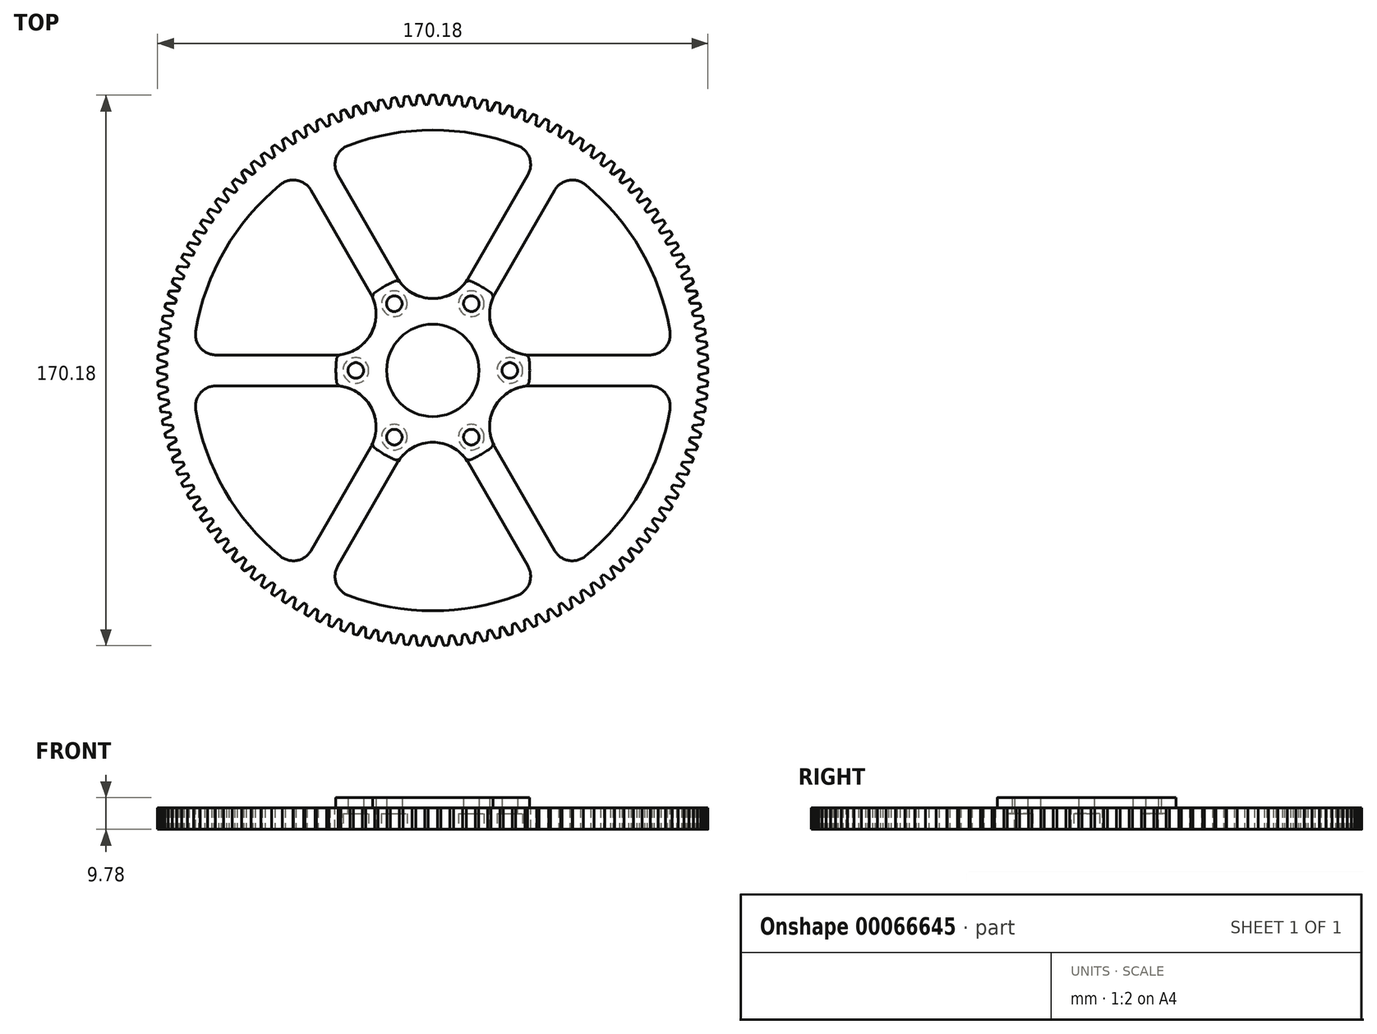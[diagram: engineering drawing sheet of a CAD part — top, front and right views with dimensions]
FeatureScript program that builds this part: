
annotation { "Feature Type Name" : "Feature", "Feature Type Description" : "" }
export const myFeature = defineFeature(function(context is Context, id is Id, definition is map)
    precondition{}
    {
        {
            var Q0;
            Q0=qCreatedBy(makeId("Top.planeOp"),FACE);
            var sketch = newSketch(context, id + "F0", { "sketchPlane" : qUnion([Q0])});
            skArc(sketch, "E0", {"start": v(-1.4, 82.23) * mm, "mid": v(-82.23, -1.4) * mm, "end": v(1.4, -82.23) * mm});
            skArc(sketch, "E1", {"start": v(1.4, -82.23) * mm, "mid": v(82.24, 0) * mm, "end": v(1.4, 82.23) * mm});
            skLineSegment(sketch, "E2", {"start": v(1.4, 82.23) * mm, "end": v(0.7, 84.97) * mm});
            skArc(sketch, "E3", {"start": v(0.7, 84.97) * mm, "mid": v(0.64, 85.06) * mm, "end": v(0.55, 85.1) * mm});
            skLineSegment(sketch, "E4", {"start": v(-1.4, 82.23) * mm, "end": v(-0.7, 84.97) * mm});
            skArc(sketch, "E5", {"start": v(-0.55, 85.1) * mm, "mid": v(-0.64, 85.06) * mm, "end": v(-0.7, 84.97) * mm});
            skLineSegment(sketch, "E6", {"start": v(-0.55, 85.1) * mm, "end": v(0.55, 85.1) * mm});
            skArc(sketch, "E7", {"start": v(1.4, 82.23) * mm, "mid": v(0, 82.24) * mm, "end": v(-1.4, 82.23) * mm});
            skSolve(sketch);
        }
        {
            var Q0;
            Q0=makeQuery(id+"F0.imprint","IMPRINT",FACE,{"disambiguationData":[TD([[makeQuery(id+"F0.imprint","IMPRINT",EDGE,{"derivedFrom":sQuery(id+"F0.wireOp",EDGE,"E0")}),1.0]])]});
            extrude(context, id + "F1", {"entities" : qUnion([Q0]), "endBound" : BoundingType.SYMMETRIC, "depth" : 6.6 * mm});
        }
        {
            var Q0;
            Q0=makeQuery(id+"F0.imprint","IMPRINT",FACE,{"disambiguationData":[TD([[makeQuery(id+"F0.imprint","IMPRINT",EDGE,{"derivedFrom":sQuery(id+"F0.wireOp",EDGE,"E2")}),1.0]])]});
            var Q1;
            Q1=makeQuery(id+"F1.opExtrude","CAP_FACE",FACE,{"disambiguationData":[OSD([sQuery(id+"F0.wireOp",EDGE,"E0"),sQuery(id+"F0.wireOp",EDGE,"E1"),sQuery(id+"F0.wireOp",EDGE,"E7")])],"isStart":false});
            var Q2;
            Q2=makeQuery(id+"F1.opExtrude","CAP_FACE",FACE,{"disambiguationData":[OSD([sQuery(id+"F0.wireOp",EDGE,"E0"),sQuery(id+"F0.wireOp",EDGE,"E1"),sQuery(id+"F0.wireOp",EDGE,"E7")])],"isStart":true});
            extrude(context, id + "F2", {"entities" : qUnion([Q0]), "endBound" : BoundingType.UP_TO_SURFACE, "endBoundEntityFace" : qUnion([Q1]), "depth" : 25.4 * mm, "hasSecondDirection" : true, "secondDirectionBound" : SecondDirectionBoundingType.UP_TO_SURFACE, "secondDirectionOppositeDirection" : true, "secondDirectionBoundEntityFace" : qUnion([Q2]), "secondDirectionDepth" : 25.4 * mm});
        }
        {
            var Q0;
            Q0=makeQuery(id+"F2.opExtrude","SWEPT_BODY",BODY,{"disambiguationData":[OSD([sQuery(id+"F0.wireOp",EDGE,"E2"),sQuery(id+"F0.wireOp",EDGE,"E3"),sQuery(id+"F0.wireOp",EDGE,"E4"),sQuery(id+"F0.wireOp",EDGE,"E5"),sQuery(id+"F0.wireOp",EDGE,"E6"),sQuery(id+"F0.wireOp",EDGE,"E7")])]});
            var Q1;
            Q1=makeQuery(id+"F1.opExtrude","CAP_EDGE",EDGE,{"disambiguationData":[OSD([sQuery(id+"F0.wireOp",EDGE,"E0"),sQuery(id+"F0.wireOp",EDGE,"E1"),sQuery(id+"F0.wireOp",EDGE,"E7")])],"isStart":false});
            circularPattern(context, id + "F3", {"operationType" : NewBodyOperationType.ADD, "entities" : qUnion([Q0]), "axis" : qUnion([Q1]), "angle" : 360 * degree, "instanceCount" : 132, "oppositeDirection" : true, "equalSpace" : true});
        }
        {
            var Q0;
            {var subQ0=sQuery(id+"F0.wireOp",EDGE,"E7");var subQ1=makeQuery(id+"F2.opExtrude","CAP_FACE",FACE,{"disambiguationData":[OSD([sQuery(id+"F0.wireOp",EDGE,"E2"),sQuery(id+"F0.wireOp",EDGE,"E3"),sQuery(id+"F0.wireOp",EDGE,"E4"),sQuery(id+"F0.wireOp",EDGE,"E5"),sQuery(id+"F0.wireOp",EDGE,"E6"),subQ0])],"isStart":false});Q0=makeQuery(id+"F3.boolean.opBoolean","MERGE",FACE,{"derivedFrom":[makeQuery(id+"F1.opExtrude","CAP_FACE",FACE,{"disambiguationData":[OSD([sQuery(id+"F0.wireOp",EDGE,"E0"),sQuery(id+"F0.wireOp",EDGE,"E1"),subQ0])],"isStart":false}),subQ1,makeQuery(id+"F3.opPattern","COPY",FACE,{"derivedFrom":subQ1,"instanceName":"1"}),makeQuery(id+"F3.opPattern","COPY",FACE,{"derivedFrom":subQ1,"instanceName":"2"}),makeQuery(id+"F3.opPattern","COPY",FACE,{"derivedFrom":subQ1,"instanceName":"3"}),makeQuery(id+"F3.opPattern","COPY",FACE,{"derivedFrom":subQ1,"instanceName":"4"}),makeQuery(id+"F3.opPattern","COPY",FACE,{"derivedFrom":subQ1,"instanceName":"5"}),makeQuery(id+"F3.opPattern","COPY",FACE,{"derivedFrom":subQ1,"instanceName":"6"}),makeQuery(id+"F3.opPattern","COPY",FACE,{"derivedFrom":subQ1,"instanceName":"7"}),makeQuery(id+"F3.opPattern","COPY",FACE,{"derivedFrom":subQ1,"instanceName":"8"}),makeQuery(id+"F3.opPattern","COPY",FACE,{"derivedFrom":subQ1,"instanceName":"9"}),makeQuery(id+"F3.opPattern","COPY",FACE,{"derivedFrom":subQ1,"instanceName":"10"}),makeQuery(id+"F3.opPattern","COPY",FACE,{"derivedFrom":subQ1,"instanceName":"11"}),makeQuery(id+"F3.opPattern","COPY",FACE,{"derivedFrom":subQ1,"instanceName":"12"}),makeQuery(id+"F3.opPattern","COPY",FACE,{"derivedFrom":subQ1,"instanceName":"13"}),makeQuery(id+"F3.opPattern","COPY",FACE,{"derivedFrom":subQ1,"instanceName":"14"}),makeQuery(id+"F3.opPattern","COPY",FACE,{"derivedFrom":subQ1,"instanceName":"15"}),makeQuery(id+"F3.opPattern","COPY",FACE,{"derivedFrom":subQ1,"instanceName":"16"}),makeQuery(id+"F3.opPattern","COPY",FACE,{"derivedFrom":subQ1,"instanceName":"17"}),makeQuery(id+"F3.opPattern","COPY",FACE,{"derivedFrom":subQ1,"instanceName":"18"}),makeQuery(id+"F3.opPattern","COPY",FACE,{"derivedFrom":subQ1,"instanceName":"19"}),makeQuery(id+"F3.opPattern","COPY",FACE,{"derivedFrom":subQ1,"instanceName":"20"}),makeQuery(id+"F3.opPattern","COPY",FACE,{"derivedFrom":subQ1,"instanceName":"21"}),makeQuery(id+"F3.opPattern","COPY",FACE,{"derivedFrom":subQ1,"instanceName":"22"}),makeQuery(id+"F3.opPattern","COPY",FACE,{"derivedFrom":subQ1,"instanceName":"23"}),makeQuery(id+"F3.opPattern","COPY",FACE,{"derivedFrom":subQ1,"instanceName":"24"}),makeQuery(id+"F3.opPattern","COPY",FACE,{"derivedFrom":subQ1,"instanceName":"25"}),makeQuery(id+"F3.opPattern","COPY",FACE,{"derivedFrom":subQ1,"instanceName":"26"}),makeQuery(id+"F3.opPattern","COPY",FACE,{"derivedFrom":subQ1,"instanceName":"27"}),makeQuery(id+"F3.opPattern","COPY",FACE,{"derivedFrom":subQ1,"instanceName":"28"}),makeQuery(id+"F3.opPattern","COPY",FACE,{"derivedFrom":subQ1,"instanceName":"29"}),makeQuery(id+"F3.opPattern","COPY",FACE,{"derivedFrom":subQ1,"instanceName":"30"}),makeQuery(id+"F3.opPattern","COPY",FACE,{"derivedFrom":subQ1,"instanceName":"31"}),makeQuery(id+"F3.opPattern","COPY",FACE,{"derivedFrom":subQ1,"instanceName":"32"}),makeQuery(id+"F3.opPattern","COPY",FACE,{"derivedFrom":subQ1,"instanceName":"33"}),makeQuery(id+"F3.opPattern","COPY",FACE,{"derivedFrom":subQ1,"instanceName":"34"}),makeQuery(id+"F3.opPattern","COPY",FACE,{"derivedFrom":subQ1,"instanceName":"35"}),makeQuery(id+"F3.opPattern","COPY",FACE,{"derivedFrom":subQ1,"instanceName":"36"}),makeQuery(id+"F3.opPattern","COPY",FACE,{"derivedFrom":subQ1,"instanceName":"37"}),makeQuery(id+"F3.opPattern","COPY",FACE,{"derivedFrom":subQ1,"instanceName":"38"}),makeQuery(id+"F3.opPattern","COPY",FACE,{"derivedFrom":subQ1,"instanceName":"39"}),makeQuery(id+"F3.opPattern","COPY",FACE,{"derivedFrom":subQ1,"instanceName":"40"}),makeQuery(id+"F3.opPattern","COPY",FACE,{"derivedFrom":subQ1,"instanceName":"41"}),makeQuery(id+"F3.opPattern","COPY",FACE,{"derivedFrom":subQ1,"instanceName":"42"}),makeQuery(id+"F3.opPattern","COPY",FACE,{"derivedFrom":subQ1,"instanceName":"43"}),makeQuery(id+"F3.opPattern","COPY",FACE,{"derivedFrom":subQ1,"instanceName":"44"}),makeQuery(id+"F3.opPattern","COPY",FACE,{"derivedFrom":subQ1,"instanceName":"45"}),makeQuery(id+"F3.opPattern","COPY",FACE,{"derivedFrom":subQ1,"instanceName":"46"}),makeQuery(id+"F3.opPattern","COPY",FACE,{"derivedFrom":subQ1,"instanceName":"47"}),makeQuery(id+"F3.opPattern","COPY",FACE,{"derivedFrom":subQ1,"instanceName":"48"}),makeQuery(id+"F3.opPattern","COPY",FACE,{"derivedFrom":subQ1,"instanceName":"49"}),makeQuery(id+"F3.opPattern","COPY",FACE,{"derivedFrom":subQ1,"instanceName":"50"}),makeQuery(id+"F3.opPattern","COPY",FACE,{"derivedFrom":subQ1,"instanceName":"51"}),makeQuery(id+"F3.opPattern","COPY",FACE,{"derivedFrom":subQ1,"instanceName":"52"}),makeQuery(id+"F3.opPattern","COPY",FACE,{"derivedFrom":subQ1,"instanceName":"53"}),makeQuery(id+"F3.opPattern","COPY",FACE,{"derivedFrom":subQ1,"instanceName":"54"}),makeQuery(id+"F3.opPattern","COPY",FACE,{"derivedFrom":subQ1,"instanceName":"55"}),makeQuery(id+"F3.opPattern","COPY",FACE,{"derivedFrom":subQ1,"instanceName":"56"}),makeQuery(id+"F3.opPattern","COPY",FACE,{"derivedFrom":subQ1,"instanceName":"57"}),makeQuery(id+"F3.opPattern","COPY",FACE,{"derivedFrom":subQ1,"instanceName":"58"}),makeQuery(id+"F3.opPattern","COPY",FACE,{"derivedFrom":subQ1,"instanceName":"59"}),makeQuery(id+"F3.opPattern","COPY",FACE,{"derivedFrom":subQ1,"instanceName":"60"}),makeQuery(id+"F3.opPattern","COPY",FACE,{"derivedFrom":subQ1,"instanceName":"61"}),makeQuery(id+"F3.opPattern","COPY",FACE,{"derivedFrom":subQ1,"instanceName":"62"}),makeQuery(id+"F3.opPattern","COPY",FACE,{"derivedFrom":subQ1,"instanceName":"63"}),makeQuery(id+"F3.opPattern","COPY",FACE,{"derivedFrom":subQ1,"instanceName":"64"}),makeQuery(id+"F3.opPattern","COPY",FACE,{"derivedFrom":subQ1,"instanceName":"65"}),makeQuery(id+"F3.opPattern","COPY",FACE,{"derivedFrom":subQ1,"instanceName":"66"}),makeQuery(id+"F3.opPattern","COPY",FACE,{"derivedFrom":subQ1,"instanceName":"67"}),makeQuery(id+"F3.opPattern","COPY",FACE,{"derivedFrom":subQ1,"instanceName":"68"}),makeQuery(id+"F3.opPattern","COPY",FACE,{"derivedFrom":subQ1,"instanceName":"69"}),makeQuery(id+"F3.opPattern","COPY",FACE,{"derivedFrom":subQ1,"instanceName":"70"}),makeQuery(id+"F3.opPattern","COPY",FACE,{"derivedFrom":subQ1,"instanceName":"71"}),makeQuery(id+"F3.opPattern","COPY",FACE,{"derivedFrom":subQ1,"instanceName":"72"}),makeQuery(id+"F3.opPattern","COPY",FACE,{"derivedFrom":subQ1,"instanceName":"73"}),makeQuery(id+"F3.opPattern","COPY",FACE,{"derivedFrom":subQ1,"instanceName":"74"}),makeQuery(id+"F3.opPattern","COPY",FACE,{"derivedFrom":subQ1,"instanceName":"75"}),makeQuery(id+"F3.opPattern","COPY",FACE,{"derivedFrom":subQ1,"instanceName":"76"}),makeQuery(id+"F3.opPattern","COPY",FACE,{"derivedFrom":subQ1,"instanceName":"77"}),makeQuery(id+"F3.opPattern","COPY",FACE,{"derivedFrom":subQ1,"instanceName":"78"}),makeQuery(id+"F3.opPattern","COPY",FACE,{"derivedFrom":subQ1,"instanceName":"79"}),makeQuery(id+"F3.opPattern","COPY",FACE,{"derivedFrom":subQ1,"instanceName":"80"}),makeQuery(id+"F3.opPattern","COPY",FACE,{"derivedFrom":subQ1,"instanceName":"81"}),makeQuery(id+"F3.opPattern","COPY",FACE,{"derivedFrom":subQ1,"instanceName":"82"}),makeQuery(id+"F3.opPattern","COPY",FACE,{"derivedFrom":subQ1,"instanceName":"83"}),makeQuery(id+"F3.opPattern","COPY",FACE,{"derivedFrom":subQ1,"instanceName":"84"}),makeQuery(id+"F3.opPattern","COPY",FACE,{"derivedFrom":subQ1,"instanceName":"85"}),makeQuery(id+"F3.opPattern","COPY",FACE,{"derivedFrom":subQ1,"instanceName":"86"}),makeQuery(id+"F3.opPattern","COPY",FACE,{"derivedFrom":subQ1,"instanceName":"87"}),makeQuery(id+"F3.opPattern","COPY",FACE,{"derivedFrom":subQ1,"instanceName":"88"}),makeQuery(id+"F3.opPattern","COPY",FACE,{"derivedFrom":subQ1,"instanceName":"89"}),makeQuery(id+"F3.opPattern","COPY",FACE,{"derivedFrom":subQ1,"instanceName":"90"}),makeQuery(id+"F3.opPattern","COPY",FACE,{"derivedFrom":subQ1,"instanceName":"91"}),makeQuery(id+"F3.opPattern","COPY",FACE,{"derivedFrom":subQ1,"instanceName":"92"}),makeQuery(id+"F3.opPattern","COPY",FACE,{"derivedFrom":subQ1,"instanceName":"93"}),makeQuery(id+"F3.opPattern","COPY",FACE,{"derivedFrom":subQ1,"instanceName":"94"}),makeQuery(id+"F3.opPattern","COPY",FACE,{"derivedFrom":subQ1,"instanceName":"95"}),makeQuery(id+"F3.opPattern","COPY",FACE,{"derivedFrom":subQ1,"instanceName":"96"}),makeQuery(id+"F3.opPattern","COPY",FACE,{"derivedFrom":subQ1,"instanceName":"97"}),makeQuery(id+"F3.opPattern","COPY",FACE,{"derivedFrom":subQ1,"instanceName":"98"}),makeQuery(id+"F3.opPattern","COPY",FACE,{"derivedFrom":subQ1,"instanceName":"99"}),makeQuery(id+"F3.opPattern","COPY",FACE,{"derivedFrom":subQ1,"instanceName":"100"}),makeQuery(id+"F3.opPattern","COPY",FACE,{"derivedFrom":subQ1,"instanceName":"101"}),makeQuery(id+"F3.opPattern","COPY",FACE,{"derivedFrom":subQ1,"instanceName":"102"}),makeQuery(id+"F3.opPattern","COPY",FACE,{"derivedFrom":subQ1,"instanceName":"103"}),makeQuery(id+"F3.opPattern","COPY",FACE,{"derivedFrom":subQ1,"instanceName":"104"}),makeQuery(id+"F3.opPattern","COPY",FACE,{"derivedFrom":subQ1,"instanceName":"105"}),makeQuery(id+"F3.opPattern","COPY",FACE,{"derivedFrom":subQ1,"instanceName":"106"}),makeQuery(id+"F3.opPattern","COPY",FACE,{"derivedFrom":subQ1,"instanceName":"107"}),makeQuery(id+"F3.opPattern","COPY",FACE,{"derivedFrom":subQ1,"instanceName":"108"}),makeQuery(id+"F3.opPattern","COPY",FACE,{"derivedFrom":subQ1,"instanceName":"109"}),makeQuery(id+"F3.opPattern","COPY",FACE,{"derivedFrom":subQ1,"instanceName":"110"}),makeQuery(id+"F3.opPattern","COPY",FACE,{"derivedFrom":subQ1,"instanceName":"111"}),makeQuery(id+"F3.opPattern","COPY",FACE,{"derivedFrom":subQ1,"instanceName":"112"}),makeQuery(id+"F3.opPattern","COPY",FACE,{"derivedFrom":subQ1,"instanceName":"113"}),makeQuery(id+"F3.opPattern","COPY",FACE,{"derivedFrom":subQ1,"instanceName":"114"}),makeQuery(id+"F3.opPattern","COPY",FACE,{"derivedFrom":subQ1,"instanceName":"115"}),makeQuery(id+"F3.opPattern","COPY",FACE,{"derivedFrom":subQ1,"instanceName":"116"}),makeQuery(id+"F3.opPattern","COPY",FACE,{"derivedFrom":subQ1,"instanceName":"117"}),makeQuery(id+"F3.opPattern","COPY",FACE,{"derivedFrom":subQ1,"instanceName":"118"}),makeQuery(id+"F3.opPattern","COPY",FACE,{"derivedFrom":subQ1,"instanceName":"119"}),makeQuery(id+"F3.opPattern","COPY",FACE,{"derivedFrom":subQ1,"instanceName":"120"}),makeQuery(id+"F3.opPattern","COPY",FACE,{"derivedFrom":subQ1,"instanceName":"121"}),makeQuery(id+"F3.opPattern","COPY",FACE,{"derivedFrom":subQ1,"instanceName":"122"}),makeQuery(id+"F3.opPattern","COPY",FACE,{"derivedFrom":subQ1,"instanceName":"123"}),makeQuery(id+"F3.opPattern","COPY",FACE,{"derivedFrom":subQ1,"instanceName":"124"}),makeQuery(id+"F3.opPattern","COPY",FACE,{"derivedFrom":subQ1,"instanceName":"125"}),makeQuery(id+"F3.opPattern","COPY",FACE,{"derivedFrom":subQ1,"instanceName":"126"}),makeQuery(id+"F3.opPattern","COPY",FACE,{"derivedFrom":subQ1,"instanceName":"127"}),makeQuery(id+"F3.opPattern","COPY",FACE,{"derivedFrom":subQ1,"instanceName":"128"}),makeQuery(id+"F3.opPattern","COPY",FACE,{"derivedFrom":subQ1,"instanceName":"129"}),makeQuery(id+"F3.opPattern","COPY",FACE,{"derivedFrom":subQ1,"instanceName":"130"}),makeQuery(id+"F3.opPattern","COPY",FACE,{"derivedFrom":subQ1,"instanceName":"131"})]});}
            var sketch = newSketch(context, id + "F4", { "sketchPlane" : qUnion([Q0])});
            skCircle(sketch, "E8", {"center": v(0, 0) * mm, "radius": 14.29 * mm});
            skCircle(sketch, "E9.cCircle", {"center": v(0, 0) * mm, "radius": 23.81 * mm, "construction": true});
            skLineSegment(sketch, "E9.0", {"start": v(23.81, 0) * mm, "end": v(11.9, -20.62) * mm, "construction": true});
            skLineSegment(sketch, "E9.1", {"start": v(11.9, -20.62) * mm, "end": v(-11.9, -20.62) * mm, "construction": true});
            skLineSegment(sketch, "E9.2", {"start": v(-11.9, -20.62) * mm, "end": v(-23.81, 0) * mm, "construction": true});
            skLineSegment(sketch, "E9.3", {"start": v(-23.81, 0) * mm, "end": v(-11.9, 20.62) * mm, "construction": true});
            skLineSegment(sketch, "E9.4", {"start": v(-11.9, 20.62) * mm, "end": v(11.9, 20.62) * mm, "construction": true});
            skLineSegment(sketch, "E9.5", {"start": v(11.9, 20.62) * mm, "end": v(23.81, 0) * mm, "construction": true});
            skCircle(sketch, "E10", {"center": v(-11.9, 20.62) * mm, "radius": 2.41 * mm});
            skCircle(sketch, "E11", {"center": v(-23.81, 0) * mm, "radius": 2.41 * mm});
            skCircle(sketch, "E12", {"center": v(-11.9, -20.62) * mm, "radius": 2.41 * mm});
            skCircle(sketch, "E13", {"center": v(11.9, -20.62) * mm, "radius": 2.41 * mm});
            skCircle(sketch, "E14", {"center": v(23.81, 0) * mm, "radius": 2.41 * mm});
            skCircle(sketch, "E15", {"center": v(11.9, 20.62) * mm, "radius": 2.41 * mm});
            skSolve(sketch);
        }
        {
            var Q0;
            Q0 = qSketchRegion(id + "F4", true);
            extrude(context, id + "F5", {"entities" : qUnion([Q0]), "operationType" : NewBodyOperationType.REMOVE, "endBound" : BoundingType.THROUGH_ALL, "oppositeDirection" : true, "depth" : 25.4 * mm});
        }
        {
            var Q0;
            {var subQ0=sQuery(id+"F0.wireOp",EDGE,"E7");var subQ1=makeQuery(id+"F2.opExtrude","CAP_FACE",FACE,{"disambiguationData":[OSD([sQuery(id+"F0.wireOp",EDGE,"E2"),sQuery(id+"F0.wireOp",EDGE,"E3"),sQuery(id+"F0.wireOp",EDGE,"E4"),sQuery(id+"F0.wireOp",EDGE,"E5"),sQuery(id+"F0.wireOp",EDGE,"E6"),subQ0])],"isStart":false});Q0=makeQuery(id+"F3.boolean.opBoolean","MERGE",FACE,{"derivedFrom":[makeQuery(id+"F1.opExtrude","CAP_FACE",FACE,{"disambiguationData":[OSD([sQuery(id+"F0.wireOp",EDGE,"E0"),sQuery(id+"F0.wireOp",EDGE,"E1"),subQ0])],"isStart":false}),subQ1,makeQuery(id+"F3.opPattern","COPY",FACE,{"derivedFrom":subQ1,"instanceName":"1"}),makeQuery(id+"F3.opPattern","COPY",FACE,{"derivedFrom":subQ1,"instanceName":"2"}),makeQuery(id+"F3.opPattern","COPY",FACE,{"derivedFrom":subQ1,"instanceName":"3"}),makeQuery(id+"F3.opPattern","COPY",FACE,{"derivedFrom":subQ1,"instanceName":"4"}),makeQuery(id+"F3.opPattern","COPY",FACE,{"derivedFrom":subQ1,"instanceName":"5"}),makeQuery(id+"F3.opPattern","COPY",FACE,{"derivedFrom":subQ1,"instanceName":"6"}),makeQuery(id+"F3.opPattern","COPY",FACE,{"derivedFrom":subQ1,"instanceName":"7"}),makeQuery(id+"F3.opPattern","COPY",FACE,{"derivedFrom":subQ1,"instanceName":"8"}),makeQuery(id+"F3.opPattern","COPY",FACE,{"derivedFrom":subQ1,"instanceName":"9"}),makeQuery(id+"F3.opPattern","COPY",FACE,{"derivedFrom":subQ1,"instanceName":"10"}),makeQuery(id+"F3.opPattern","COPY",FACE,{"derivedFrom":subQ1,"instanceName":"11"}),makeQuery(id+"F3.opPattern","COPY",FACE,{"derivedFrom":subQ1,"instanceName":"12"}),makeQuery(id+"F3.opPattern","COPY",FACE,{"derivedFrom":subQ1,"instanceName":"13"}),makeQuery(id+"F3.opPattern","COPY",FACE,{"derivedFrom":subQ1,"instanceName":"14"}),makeQuery(id+"F3.opPattern","COPY",FACE,{"derivedFrom":subQ1,"instanceName":"15"}),makeQuery(id+"F3.opPattern","COPY",FACE,{"derivedFrom":subQ1,"instanceName":"16"}),makeQuery(id+"F3.opPattern","COPY",FACE,{"derivedFrom":subQ1,"instanceName":"17"}),makeQuery(id+"F3.opPattern","COPY",FACE,{"derivedFrom":subQ1,"instanceName":"18"}),makeQuery(id+"F3.opPattern","COPY",FACE,{"derivedFrom":subQ1,"instanceName":"19"}),makeQuery(id+"F3.opPattern","COPY",FACE,{"derivedFrom":subQ1,"instanceName":"20"}),makeQuery(id+"F3.opPattern","COPY",FACE,{"derivedFrom":subQ1,"instanceName":"21"}),makeQuery(id+"F3.opPattern","COPY",FACE,{"derivedFrom":subQ1,"instanceName":"22"}),makeQuery(id+"F3.opPattern","COPY",FACE,{"derivedFrom":subQ1,"instanceName":"23"}),makeQuery(id+"F3.opPattern","COPY",FACE,{"derivedFrom":subQ1,"instanceName":"24"}),makeQuery(id+"F3.opPattern","COPY",FACE,{"derivedFrom":subQ1,"instanceName":"25"}),makeQuery(id+"F3.opPattern","COPY",FACE,{"derivedFrom":subQ1,"instanceName":"26"}),makeQuery(id+"F3.opPattern","COPY",FACE,{"derivedFrom":subQ1,"instanceName":"27"}),makeQuery(id+"F3.opPattern","COPY",FACE,{"derivedFrom":subQ1,"instanceName":"28"}),makeQuery(id+"F3.opPattern","COPY",FACE,{"derivedFrom":subQ1,"instanceName":"29"}),makeQuery(id+"F3.opPattern","COPY",FACE,{"derivedFrom":subQ1,"instanceName":"30"}),makeQuery(id+"F3.opPattern","COPY",FACE,{"derivedFrom":subQ1,"instanceName":"31"}),makeQuery(id+"F3.opPattern","COPY",FACE,{"derivedFrom":subQ1,"instanceName":"32"}),makeQuery(id+"F3.opPattern","COPY",FACE,{"derivedFrom":subQ1,"instanceName":"33"}),makeQuery(id+"F3.opPattern","COPY",FACE,{"derivedFrom":subQ1,"instanceName":"34"}),makeQuery(id+"F3.opPattern","COPY",FACE,{"derivedFrom":subQ1,"instanceName":"35"}),makeQuery(id+"F3.opPattern","COPY",FACE,{"derivedFrom":subQ1,"instanceName":"36"}),makeQuery(id+"F3.opPattern","COPY",FACE,{"derivedFrom":subQ1,"instanceName":"37"}),makeQuery(id+"F3.opPattern","COPY",FACE,{"derivedFrom":subQ1,"instanceName":"38"}),makeQuery(id+"F3.opPattern","COPY",FACE,{"derivedFrom":subQ1,"instanceName":"39"}),makeQuery(id+"F3.opPattern","COPY",FACE,{"derivedFrom":subQ1,"instanceName":"40"}),makeQuery(id+"F3.opPattern","COPY",FACE,{"derivedFrom":subQ1,"instanceName":"41"}),makeQuery(id+"F3.opPattern","COPY",FACE,{"derivedFrom":subQ1,"instanceName":"42"}),makeQuery(id+"F3.opPattern","COPY",FACE,{"derivedFrom":subQ1,"instanceName":"43"}),makeQuery(id+"F3.opPattern","COPY",FACE,{"derivedFrom":subQ1,"instanceName":"44"}),makeQuery(id+"F3.opPattern","COPY",FACE,{"derivedFrom":subQ1,"instanceName":"45"}),makeQuery(id+"F3.opPattern","COPY",FACE,{"derivedFrom":subQ1,"instanceName":"46"}),makeQuery(id+"F3.opPattern","COPY",FACE,{"derivedFrom":subQ1,"instanceName":"47"}),makeQuery(id+"F3.opPattern","COPY",FACE,{"derivedFrom":subQ1,"instanceName":"48"}),makeQuery(id+"F3.opPattern","COPY",FACE,{"derivedFrom":subQ1,"instanceName":"49"}),makeQuery(id+"F3.opPattern","COPY",FACE,{"derivedFrom":subQ1,"instanceName":"50"}),makeQuery(id+"F3.opPattern","COPY",FACE,{"derivedFrom":subQ1,"instanceName":"51"}),makeQuery(id+"F3.opPattern","COPY",FACE,{"derivedFrom":subQ1,"instanceName":"52"}),makeQuery(id+"F3.opPattern","COPY",FACE,{"derivedFrom":subQ1,"instanceName":"53"}),makeQuery(id+"F3.opPattern","COPY",FACE,{"derivedFrom":subQ1,"instanceName":"54"}),makeQuery(id+"F3.opPattern","COPY",FACE,{"derivedFrom":subQ1,"instanceName":"55"}),makeQuery(id+"F3.opPattern","COPY",FACE,{"derivedFrom":subQ1,"instanceName":"56"}),makeQuery(id+"F3.opPattern","COPY",FACE,{"derivedFrom":subQ1,"instanceName":"57"}),makeQuery(id+"F3.opPattern","COPY",FACE,{"derivedFrom":subQ1,"instanceName":"58"}),makeQuery(id+"F3.opPattern","COPY",FACE,{"derivedFrom":subQ1,"instanceName":"59"}),makeQuery(id+"F3.opPattern","COPY",FACE,{"derivedFrom":subQ1,"instanceName":"60"}),makeQuery(id+"F3.opPattern","COPY",FACE,{"derivedFrom":subQ1,"instanceName":"61"}),makeQuery(id+"F3.opPattern","COPY",FACE,{"derivedFrom":subQ1,"instanceName":"62"}),makeQuery(id+"F3.opPattern","COPY",FACE,{"derivedFrom":subQ1,"instanceName":"63"}),makeQuery(id+"F3.opPattern","COPY",FACE,{"derivedFrom":subQ1,"instanceName":"64"}),makeQuery(id+"F3.opPattern","COPY",FACE,{"derivedFrom":subQ1,"instanceName":"65"}),makeQuery(id+"F3.opPattern","COPY",FACE,{"derivedFrom":subQ1,"instanceName":"66"}),makeQuery(id+"F3.opPattern","COPY",FACE,{"derivedFrom":subQ1,"instanceName":"67"}),makeQuery(id+"F3.opPattern","COPY",FACE,{"derivedFrom":subQ1,"instanceName":"68"}),makeQuery(id+"F3.opPattern","COPY",FACE,{"derivedFrom":subQ1,"instanceName":"69"}),makeQuery(id+"F3.opPattern","COPY",FACE,{"derivedFrom":subQ1,"instanceName":"70"}),makeQuery(id+"F3.opPattern","COPY",FACE,{"derivedFrom":subQ1,"instanceName":"71"}),makeQuery(id+"F3.opPattern","COPY",FACE,{"derivedFrom":subQ1,"instanceName":"72"}),makeQuery(id+"F3.opPattern","COPY",FACE,{"derivedFrom":subQ1,"instanceName":"73"}),makeQuery(id+"F3.opPattern","COPY",FACE,{"derivedFrom":subQ1,"instanceName":"74"}),makeQuery(id+"F3.opPattern","COPY",FACE,{"derivedFrom":subQ1,"instanceName":"75"}),makeQuery(id+"F3.opPattern","COPY",FACE,{"derivedFrom":subQ1,"instanceName":"76"}),makeQuery(id+"F3.opPattern","COPY",FACE,{"derivedFrom":subQ1,"instanceName":"77"}),makeQuery(id+"F3.opPattern","COPY",FACE,{"derivedFrom":subQ1,"instanceName":"78"}),makeQuery(id+"F3.opPattern","COPY",FACE,{"derivedFrom":subQ1,"instanceName":"79"}),makeQuery(id+"F3.opPattern","COPY",FACE,{"derivedFrom":subQ1,"instanceName":"80"}),makeQuery(id+"F3.opPattern","COPY",FACE,{"derivedFrom":subQ1,"instanceName":"81"}),makeQuery(id+"F3.opPattern","COPY",FACE,{"derivedFrom":subQ1,"instanceName":"82"}),makeQuery(id+"F3.opPattern","COPY",FACE,{"derivedFrom":subQ1,"instanceName":"83"}),makeQuery(id+"F3.opPattern","COPY",FACE,{"derivedFrom":subQ1,"instanceName":"84"}),makeQuery(id+"F3.opPattern","COPY",FACE,{"derivedFrom":subQ1,"instanceName":"85"}),makeQuery(id+"F3.opPattern","COPY",FACE,{"derivedFrom":subQ1,"instanceName":"86"}),makeQuery(id+"F3.opPattern","COPY",FACE,{"derivedFrom":subQ1,"instanceName":"87"}),makeQuery(id+"F3.opPattern","COPY",FACE,{"derivedFrom":subQ1,"instanceName":"88"}),makeQuery(id+"F3.opPattern","COPY",FACE,{"derivedFrom":subQ1,"instanceName":"89"}),makeQuery(id+"F3.opPattern","COPY",FACE,{"derivedFrom":subQ1,"instanceName":"90"}),makeQuery(id+"F3.opPattern","COPY",FACE,{"derivedFrom":subQ1,"instanceName":"91"}),makeQuery(id+"F3.opPattern","COPY",FACE,{"derivedFrom":subQ1,"instanceName":"92"}),makeQuery(id+"F3.opPattern","COPY",FACE,{"derivedFrom":subQ1,"instanceName":"93"}),makeQuery(id+"F3.opPattern","COPY",FACE,{"derivedFrom":subQ1,"instanceName":"94"}),makeQuery(id+"F3.opPattern","COPY",FACE,{"derivedFrom":subQ1,"instanceName":"95"}),makeQuery(id+"F3.opPattern","COPY",FACE,{"derivedFrom":subQ1,"instanceName":"96"}),makeQuery(id+"F3.opPattern","COPY",FACE,{"derivedFrom":subQ1,"instanceName":"97"}),makeQuery(id+"F3.opPattern","COPY",FACE,{"derivedFrom":subQ1,"instanceName":"98"}),makeQuery(id+"F3.opPattern","COPY",FACE,{"derivedFrom":subQ1,"instanceName":"99"}),makeQuery(id+"F3.opPattern","COPY",FACE,{"derivedFrom":subQ1,"instanceName":"100"}),makeQuery(id+"F3.opPattern","COPY",FACE,{"derivedFrom":subQ1,"instanceName":"101"}),makeQuery(id+"F3.opPattern","COPY",FACE,{"derivedFrom":subQ1,"instanceName":"102"}),makeQuery(id+"F3.opPattern","COPY",FACE,{"derivedFrom":subQ1,"instanceName":"103"}),makeQuery(id+"F3.opPattern","COPY",FACE,{"derivedFrom":subQ1,"instanceName":"104"}),makeQuery(id+"F3.opPattern","COPY",FACE,{"derivedFrom":subQ1,"instanceName":"105"}),makeQuery(id+"F3.opPattern","COPY",FACE,{"derivedFrom":subQ1,"instanceName":"106"}),makeQuery(id+"F3.opPattern","COPY",FACE,{"derivedFrom":subQ1,"instanceName":"107"}),makeQuery(id+"F3.opPattern","COPY",FACE,{"derivedFrom":subQ1,"instanceName":"108"}),makeQuery(id+"F3.opPattern","COPY",FACE,{"derivedFrom":subQ1,"instanceName":"109"}),makeQuery(id+"F3.opPattern","COPY",FACE,{"derivedFrom":subQ1,"instanceName":"110"}),makeQuery(id+"F3.opPattern","COPY",FACE,{"derivedFrom":subQ1,"instanceName":"111"}),makeQuery(id+"F3.opPattern","COPY",FACE,{"derivedFrom":subQ1,"instanceName":"112"}),makeQuery(id+"F3.opPattern","COPY",FACE,{"derivedFrom":subQ1,"instanceName":"113"}),makeQuery(id+"F3.opPattern","COPY",FACE,{"derivedFrom":subQ1,"instanceName":"114"}),makeQuery(id+"F3.opPattern","COPY",FACE,{"derivedFrom":subQ1,"instanceName":"115"}),makeQuery(id+"F3.opPattern","COPY",FACE,{"derivedFrom":subQ1,"instanceName":"116"}),makeQuery(id+"F3.opPattern","COPY",FACE,{"derivedFrom":subQ1,"instanceName":"117"}),makeQuery(id+"F3.opPattern","COPY",FACE,{"derivedFrom":subQ1,"instanceName":"118"}),makeQuery(id+"F3.opPattern","COPY",FACE,{"derivedFrom":subQ1,"instanceName":"119"}),makeQuery(id+"F3.opPattern","COPY",FACE,{"derivedFrom":subQ1,"instanceName":"120"}),makeQuery(id+"F3.opPattern","COPY",FACE,{"derivedFrom":subQ1,"instanceName":"121"}),makeQuery(id+"F3.opPattern","COPY",FACE,{"derivedFrom":subQ1,"instanceName":"122"}),makeQuery(id+"F3.opPattern","COPY",FACE,{"derivedFrom":subQ1,"instanceName":"123"}),makeQuery(id+"F3.opPattern","COPY",FACE,{"derivedFrom":subQ1,"instanceName":"124"}),makeQuery(id+"F3.opPattern","COPY",FACE,{"derivedFrom":subQ1,"instanceName":"125"}),makeQuery(id+"F3.opPattern","COPY",FACE,{"derivedFrom":subQ1,"instanceName":"126"}),makeQuery(id+"F3.opPattern","COPY",FACE,{"derivedFrom":subQ1,"instanceName":"127"}),makeQuery(id+"F3.opPattern","COPY",FACE,{"derivedFrom":subQ1,"instanceName":"128"}),makeQuery(id+"F3.opPattern","COPY",FACE,{"derivedFrom":subQ1,"instanceName":"129"}),makeQuery(id+"F3.opPattern","COPY",FACE,{"derivedFrom":subQ1,"instanceName":"130"}),makeQuery(id+"F3.opPattern","COPY",FACE,{"derivedFrom":subQ1,"instanceName":"131"})]});}
            var sketch = newSketch(context, id + "F6", { "sketchPlane" : qUnion([Q0])});
            skArc(sketch, "E16", {"start": v(-37.15, 64.35) * mm, "mid": v(-64.35, 37.15) * mm, "end": v(-74.3, 0) * mm});
            skArc(sketch, "E17", {"start": v(-15.08, 26.12) * mm, "mid": v(-26.12, 15.08) * mm, "end": v(-30.16, 0) * mm});
            skLineSegment(sketch, "E18", {"start": v(-15.08, 26.12) * mm, "end": v(-37.15, 64.35) * mm, "construction": true});
            skLineSegment(sketch, "E19", {"start": v(-30.16, 0) * mm, "end": v(-74.3, 0) * mm, "construction": true});
            skPoint(sketch, "E20", {"position": v(-23.81, 0) * mm});
            skLineSegment(sketch, "E21.0", {"start": v(-29.78, 4.77) * mm, "end": v(-74.15, 4.77) * mm});
            skLineSegment(sketch, "E22.0", {"start": v(-19.02, 23.4) * mm, "end": v(-41.2, 61.83) * mm});
            skPoint(sketch, "E23", {"position": v(-11.9, 20.62) * mm});
            skArc(sketch, "E24", {"start": v(-29.78, 4.77) * mm, "mid": v(-19.25, 11.11) * mm, "end": v(-19.02, 23.4) * mm});
            skCircle(sketch, "E25", {"center": v(0, 0) * mm, "radius": 34.93 * mm, "construction": true});
            skLineSegment(sketch, "E26", {"start": v(-26.12, 15.08) * mm, "end": v(0, 0) * mm, "construction": true});
            skSolve(sketch);
        }
        {
            var Q0;
            {var subQ0=sQuery(id+"F6.wireOp",EDGE,"E21.0");Q0=makeQuery(id+"F6.imprint","IMPRINT",FACE,{"disambiguationData":[TD([[makeQuery(id+"F6.imprint","IMPRINT",EDGE,{"derivedFrom":subQ0}),-1.0]])]});}
            var Q1;
            {var subQ0=sQuery(id+"F6.wireOp",EDGE,"E24");Q1=makeQuery(id+"F6.imprint","IMPRINT",FACE,{"disambiguationData":[TD([[makeQuery(id+"F6.imprint","IMPRINT",EDGE,{"derivedFrom":subQ0}),1.0]])]});}
            var Q2;
            {var subQ0=sQuery(id+"F0.wireOp",EDGE,"E7");var subQ1=makeQuery(id+"F2.opExtrude","CAP_FACE",FACE,{"disambiguationData":[OSD([sQuery(id+"F0.wireOp",EDGE,"E2"),sQuery(id+"F0.wireOp",EDGE,"E3"),sQuery(id+"F0.wireOp",EDGE,"E4"),sQuery(id+"F0.wireOp",EDGE,"E5"),sQuery(id+"F0.wireOp",EDGE,"E6"),subQ0])],"isStart":true});Q2=makeQuery(id+"F3.boolean.opBoolean","MERGE",FACE,{"derivedFrom":[makeQuery(id+"F1.opExtrude","CAP_FACE",FACE,{"disambiguationData":[OSD([sQuery(id+"F0.wireOp",EDGE,"E0"),sQuery(id+"F0.wireOp",EDGE,"E1"),subQ0])],"isStart":true}),subQ1,makeQuery(id+"F3.opPattern","COPY",FACE,{"derivedFrom":subQ1,"instanceName":"1"}),makeQuery(id+"F3.opPattern","COPY",FACE,{"derivedFrom":subQ1,"instanceName":"2"}),makeQuery(id+"F3.opPattern","COPY",FACE,{"derivedFrom":subQ1,"instanceName":"3"}),makeQuery(id+"F3.opPattern","COPY",FACE,{"derivedFrom":subQ1,"instanceName":"4"}),makeQuery(id+"F3.opPattern","COPY",FACE,{"derivedFrom":subQ1,"instanceName":"5"}),makeQuery(id+"F3.opPattern","COPY",FACE,{"derivedFrom":subQ1,"instanceName":"6"}),makeQuery(id+"F3.opPattern","COPY",FACE,{"derivedFrom":subQ1,"instanceName":"7"}),makeQuery(id+"F3.opPattern","COPY",FACE,{"derivedFrom":subQ1,"instanceName":"8"}),makeQuery(id+"F3.opPattern","COPY",FACE,{"derivedFrom":subQ1,"instanceName":"9"}),makeQuery(id+"F3.opPattern","COPY",FACE,{"derivedFrom":subQ1,"instanceName":"10"}),makeQuery(id+"F3.opPattern","COPY",FACE,{"derivedFrom":subQ1,"instanceName":"11"}),makeQuery(id+"F3.opPattern","COPY",FACE,{"derivedFrom":subQ1,"instanceName":"12"}),makeQuery(id+"F3.opPattern","COPY",FACE,{"derivedFrom":subQ1,"instanceName":"13"}),makeQuery(id+"F3.opPattern","COPY",FACE,{"derivedFrom":subQ1,"instanceName":"14"}),makeQuery(id+"F3.opPattern","COPY",FACE,{"derivedFrom":subQ1,"instanceName":"15"}),makeQuery(id+"F3.opPattern","COPY",FACE,{"derivedFrom":subQ1,"instanceName":"16"}),makeQuery(id+"F3.opPattern","COPY",FACE,{"derivedFrom":subQ1,"instanceName":"17"}),makeQuery(id+"F3.opPattern","COPY",FACE,{"derivedFrom":subQ1,"instanceName":"18"}),makeQuery(id+"F3.opPattern","COPY",FACE,{"derivedFrom":subQ1,"instanceName":"19"}),makeQuery(id+"F3.opPattern","COPY",FACE,{"derivedFrom":subQ1,"instanceName":"20"}),makeQuery(id+"F3.opPattern","COPY",FACE,{"derivedFrom":subQ1,"instanceName":"21"}),makeQuery(id+"F3.opPattern","COPY",FACE,{"derivedFrom":subQ1,"instanceName":"22"}),makeQuery(id+"F3.opPattern","COPY",FACE,{"derivedFrom":subQ1,"instanceName":"23"}),makeQuery(id+"F3.opPattern","COPY",FACE,{"derivedFrom":subQ1,"instanceName":"24"}),makeQuery(id+"F3.opPattern","COPY",FACE,{"derivedFrom":subQ1,"instanceName":"25"}),makeQuery(id+"F3.opPattern","COPY",FACE,{"derivedFrom":subQ1,"instanceName":"26"}),makeQuery(id+"F3.opPattern","COPY",FACE,{"derivedFrom":subQ1,"instanceName":"27"}),makeQuery(id+"F3.opPattern","COPY",FACE,{"derivedFrom":subQ1,"instanceName":"28"}),makeQuery(id+"F3.opPattern","COPY",FACE,{"derivedFrom":subQ1,"instanceName":"29"}),makeQuery(id+"F3.opPattern","COPY",FACE,{"derivedFrom":subQ1,"instanceName":"30"}),makeQuery(id+"F3.opPattern","COPY",FACE,{"derivedFrom":subQ1,"instanceName":"31"}),makeQuery(id+"F3.opPattern","COPY",FACE,{"derivedFrom":subQ1,"instanceName":"32"}),makeQuery(id+"F3.opPattern","COPY",FACE,{"derivedFrom":subQ1,"instanceName":"33"}),makeQuery(id+"F3.opPattern","COPY",FACE,{"derivedFrom":subQ1,"instanceName":"34"}),makeQuery(id+"F3.opPattern","COPY",FACE,{"derivedFrom":subQ1,"instanceName":"35"}),makeQuery(id+"F3.opPattern","COPY",FACE,{"derivedFrom":subQ1,"instanceName":"36"}),makeQuery(id+"F3.opPattern","COPY",FACE,{"derivedFrom":subQ1,"instanceName":"37"}),makeQuery(id+"F3.opPattern","COPY",FACE,{"derivedFrom":subQ1,"instanceName":"38"}),makeQuery(id+"F3.opPattern","COPY",FACE,{"derivedFrom":subQ1,"instanceName":"39"}),makeQuery(id+"F3.opPattern","COPY",FACE,{"derivedFrom":subQ1,"instanceName":"40"}),makeQuery(id+"F3.opPattern","COPY",FACE,{"derivedFrom":subQ1,"instanceName":"41"}),makeQuery(id+"F3.opPattern","COPY",FACE,{"derivedFrom":subQ1,"instanceName":"42"}),makeQuery(id+"F3.opPattern","COPY",FACE,{"derivedFrom":subQ1,"instanceName":"43"}),makeQuery(id+"F3.opPattern","COPY",FACE,{"derivedFrom":subQ1,"instanceName":"44"}),makeQuery(id+"F3.opPattern","COPY",FACE,{"derivedFrom":subQ1,"instanceName":"45"}),makeQuery(id+"F3.opPattern","COPY",FACE,{"derivedFrom":subQ1,"instanceName":"46"}),makeQuery(id+"F3.opPattern","COPY",FACE,{"derivedFrom":subQ1,"instanceName":"47"}),makeQuery(id+"F3.opPattern","COPY",FACE,{"derivedFrom":subQ1,"instanceName":"48"}),makeQuery(id+"F3.opPattern","COPY",FACE,{"derivedFrom":subQ1,"instanceName":"49"}),makeQuery(id+"F3.opPattern","COPY",FACE,{"derivedFrom":subQ1,"instanceName":"50"}),makeQuery(id+"F3.opPattern","COPY",FACE,{"derivedFrom":subQ1,"instanceName":"51"}),makeQuery(id+"F3.opPattern","COPY",FACE,{"derivedFrom":subQ1,"instanceName":"52"}),makeQuery(id+"F3.opPattern","COPY",FACE,{"derivedFrom":subQ1,"instanceName":"53"}),makeQuery(id+"F3.opPattern","COPY",FACE,{"derivedFrom":subQ1,"instanceName":"54"}),makeQuery(id+"F3.opPattern","COPY",FACE,{"derivedFrom":subQ1,"instanceName":"55"}),makeQuery(id+"F3.opPattern","COPY",FACE,{"derivedFrom":subQ1,"instanceName":"56"}),makeQuery(id+"F3.opPattern","COPY",FACE,{"derivedFrom":subQ1,"instanceName":"57"}),makeQuery(id+"F3.opPattern","COPY",FACE,{"derivedFrom":subQ1,"instanceName":"58"}),makeQuery(id+"F3.opPattern","COPY",FACE,{"derivedFrom":subQ1,"instanceName":"59"}),makeQuery(id+"F3.opPattern","COPY",FACE,{"derivedFrom":subQ1,"instanceName":"60"}),makeQuery(id+"F3.opPattern","COPY",FACE,{"derivedFrom":subQ1,"instanceName":"61"}),makeQuery(id+"F3.opPattern","COPY",FACE,{"derivedFrom":subQ1,"instanceName":"62"}),makeQuery(id+"F3.opPattern","COPY",FACE,{"derivedFrom":subQ1,"instanceName":"63"}),makeQuery(id+"F3.opPattern","COPY",FACE,{"derivedFrom":subQ1,"instanceName":"64"}),makeQuery(id+"F3.opPattern","COPY",FACE,{"derivedFrom":subQ1,"instanceName":"65"}),makeQuery(id+"F3.opPattern","COPY",FACE,{"derivedFrom":subQ1,"instanceName":"66"}),makeQuery(id+"F3.opPattern","COPY",FACE,{"derivedFrom":subQ1,"instanceName":"67"}),makeQuery(id+"F3.opPattern","COPY",FACE,{"derivedFrom":subQ1,"instanceName":"68"}),makeQuery(id+"F3.opPattern","COPY",FACE,{"derivedFrom":subQ1,"instanceName":"69"}),makeQuery(id+"F3.opPattern","COPY",FACE,{"derivedFrom":subQ1,"instanceName":"70"}),makeQuery(id+"F3.opPattern","COPY",FACE,{"derivedFrom":subQ1,"instanceName":"71"}),makeQuery(id+"F3.opPattern","COPY",FACE,{"derivedFrom":subQ1,"instanceName":"72"}),makeQuery(id+"F3.opPattern","COPY",FACE,{"derivedFrom":subQ1,"instanceName":"73"}),makeQuery(id+"F3.opPattern","COPY",FACE,{"derivedFrom":subQ1,"instanceName":"74"}),makeQuery(id+"F3.opPattern","COPY",FACE,{"derivedFrom":subQ1,"instanceName":"75"}),makeQuery(id+"F3.opPattern","COPY",FACE,{"derivedFrom":subQ1,"instanceName":"76"}),makeQuery(id+"F3.opPattern","COPY",FACE,{"derivedFrom":subQ1,"instanceName":"77"}),makeQuery(id+"F3.opPattern","COPY",FACE,{"derivedFrom":subQ1,"instanceName":"78"}),makeQuery(id+"F3.opPattern","COPY",FACE,{"derivedFrom":subQ1,"instanceName":"79"}),makeQuery(id+"F3.opPattern","COPY",FACE,{"derivedFrom":subQ1,"instanceName":"80"}),makeQuery(id+"F3.opPattern","COPY",FACE,{"derivedFrom":subQ1,"instanceName":"81"}),makeQuery(id+"F3.opPattern","COPY",FACE,{"derivedFrom":subQ1,"instanceName":"82"}),makeQuery(id+"F3.opPattern","COPY",FACE,{"derivedFrom":subQ1,"instanceName":"83"}),makeQuery(id+"F3.opPattern","COPY",FACE,{"derivedFrom":subQ1,"instanceName":"84"}),makeQuery(id+"F3.opPattern","COPY",FACE,{"derivedFrom":subQ1,"instanceName":"85"}),makeQuery(id+"F3.opPattern","COPY",FACE,{"derivedFrom":subQ1,"instanceName":"86"}),makeQuery(id+"F3.opPattern","COPY",FACE,{"derivedFrom":subQ1,"instanceName":"87"}),makeQuery(id+"F3.opPattern","COPY",FACE,{"derivedFrom":subQ1,"instanceName":"88"}),makeQuery(id+"F3.opPattern","COPY",FACE,{"derivedFrom":subQ1,"instanceName":"89"}),makeQuery(id+"F3.opPattern","COPY",FACE,{"derivedFrom":subQ1,"instanceName":"90"}),makeQuery(id+"F3.opPattern","COPY",FACE,{"derivedFrom":subQ1,"instanceName":"91"}),makeQuery(id+"F3.opPattern","COPY",FACE,{"derivedFrom":subQ1,"instanceName":"92"}),makeQuery(id+"F3.opPattern","COPY",FACE,{"derivedFrom":subQ1,"instanceName":"93"}),makeQuery(id+"F3.opPattern","COPY",FACE,{"derivedFrom":subQ1,"instanceName":"94"}),makeQuery(id+"F3.opPattern","COPY",FACE,{"derivedFrom":subQ1,"instanceName":"95"}),makeQuery(id+"F3.opPattern","COPY",FACE,{"derivedFrom":subQ1,"instanceName":"96"}),makeQuery(id+"F3.opPattern","COPY",FACE,{"derivedFrom":subQ1,"instanceName":"97"}),makeQuery(id+"F3.opPattern","COPY",FACE,{"derivedFrom":subQ1,"instanceName":"98"}),makeQuery(id+"F3.opPattern","COPY",FACE,{"derivedFrom":subQ1,"instanceName":"99"}),makeQuery(id+"F3.opPattern","COPY",FACE,{"derivedFrom":subQ1,"instanceName":"100"}),makeQuery(id+"F3.opPattern","COPY",FACE,{"derivedFrom":subQ1,"instanceName":"101"}),makeQuery(id+"F3.opPattern","COPY",FACE,{"derivedFrom":subQ1,"instanceName":"102"}),makeQuery(id+"F3.opPattern","COPY",FACE,{"derivedFrom":subQ1,"instanceName":"103"}),makeQuery(id+"F3.opPattern","COPY",FACE,{"derivedFrom":subQ1,"instanceName":"104"}),makeQuery(id+"F3.opPattern","COPY",FACE,{"derivedFrom":subQ1,"instanceName":"105"}),makeQuery(id+"F3.opPattern","COPY",FACE,{"derivedFrom":subQ1,"instanceName":"106"}),makeQuery(id+"F3.opPattern","COPY",FACE,{"derivedFrom":subQ1,"instanceName":"107"}),makeQuery(id+"F3.opPattern","COPY",FACE,{"derivedFrom":subQ1,"instanceName":"108"}),makeQuery(id+"F3.opPattern","COPY",FACE,{"derivedFrom":subQ1,"instanceName":"109"}),makeQuery(id+"F3.opPattern","COPY",FACE,{"derivedFrom":subQ1,"instanceName":"110"}),makeQuery(id+"F3.opPattern","COPY",FACE,{"derivedFrom":subQ1,"instanceName":"111"}),makeQuery(id+"F3.opPattern","COPY",FACE,{"derivedFrom":subQ1,"instanceName":"112"}),makeQuery(id+"F3.opPattern","COPY",FACE,{"derivedFrom":subQ1,"instanceName":"113"}),makeQuery(id+"F3.opPattern","COPY",FACE,{"derivedFrom":subQ1,"instanceName":"114"}),makeQuery(id+"F3.opPattern","COPY",FACE,{"derivedFrom":subQ1,"instanceName":"115"}),makeQuery(id+"F3.opPattern","COPY",FACE,{"derivedFrom":subQ1,"instanceName":"116"}),makeQuery(id+"F3.opPattern","COPY",FACE,{"derivedFrom":subQ1,"instanceName":"117"}),makeQuery(id+"F3.opPattern","COPY",FACE,{"derivedFrom":subQ1,"instanceName":"118"}),makeQuery(id+"F3.opPattern","COPY",FACE,{"derivedFrom":subQ1,"instanceName":"119"}),makeQuery(id+"F3.opPattern","COPY",FACE,{"derivedFrom":subQ1,"instanceName":"120"}),makeQuery(id+"F3.opPattern","COPY",FACE,{"derivedFrom":subQ1,"instanceName":"121"}),makeQuery(id+"F3.opPattern","COPY",FACE,{"derivedFrom":subQ1,"instanceName":"122"}),makeQuery(id+"F3.opPattern","COPY",FACE,{"derivedFrom":subQ1,"instanceName":"123"}),makeQuery(id+"F3.opPattern","COPY",FACE,{"derivedFrom":subQ1,"instanceName":"124"}),makeQuery(id+"F3.opPattern","COPY",FACE,{"derivedFrom":subQ1,"instanceName":"125"}),makeQuery(id+"F3.opPattern","COPY",FACE,{"derivedFrom":subQ1,"instanceName":"126"}),makeQuery(id+"F3.opPattern","COPY",FACE,{"derivedFrom":subQ1,"instanceName":"127"}),makeQuery(id+"F3.opPattern","COPY",FACE,{"derivedFrom":subQ1,"instanceName":"128"}),makeQuery(id+"F3.opPattern","COPY",FACE,{"derivedFrom":subQ1,"instanceName":"129"}),makeQuery(id+"F3.opPattern","COPY",FACE,{"derivedFrom":subQ1,"instanceName":"130"}),makeQuery(id+"F3.opPattern","COPY",FACE,{"derivedFrom":subQ1,"instanceName":"131"})]});}
            extrude(context, id + "F7", {"entities" : qUnion([Q0, Q1]), "endBound" : BoundingType.UP_TO_SURFACE, "oppositeDirection" : true, "endBoundEntityFace" : qUnion([Q2]), "depth" : 25.4 * mm});
        }
        {
            var Q0;
            Q0=makeQuery(id+"F7.opExtrude","SWEPT_EDGE",EDGE,{"disambiguationData":[OSD([sQuery(id+"F6.wireOp",EDGE,"E16"),sQuery(id+"F6.wireOp",EDGE,"E21.0")])]});
            var Q1;
            Q1=makeQuery(id+"F7.opExtrude","SWEPT_EDGE",EDGE,{"disambiguationData":[OSD([sQuery(id+"F6.wireOp",EDGE,"E17"),sQuery(id+"F6.wireOp",EDGE,"E21.0")])]});
            var Q2;
            Q2=makeQuery(id+"F7.opExtrude","SWEPT_EDGE",EDGE,{"disambiguationData":[OSD([sQuery(id+"F6.wireOp",EDGE,"E17"),sQuery(id+"F6.wireOp",EDGE,"E22.0")])]});
            var Q3;
            Q3=makeQuery(id+"F7.opExtrude","SWEPT_EDGE",EDGE,{"disambiguationData":[OSD([sQuery(id+"F6.wireOp",EDGE,"E16"),sQuery(id+"F6.wireOp",EDGE,"E22.0")])]});
            fillet(context, id + "F8", {"entities" : qUnion([Q0, Q1, Q2, Q3]), "radius" : 6.35 * mm, "tangentPropagation" : true, "allowEdgeOverflow" : false});
        }
        {
            var Q0;
            Q0=makeQuery(id+"F7.opExtrude","SWEPT_BODY",BODY,{"disambiguationData":[OSD([sQuery(id+"F6.wireOp",EDGE,"E16"),sQuery(id+"F6.wireOp",EDGE,"E17"),sQuery(id+"F6.wireOp",EDGE,"E21.0"),sQuery(id+"F6.wireOp",EDGE,"E22.0")])]});
            var Q1;
            Q1=makeQuery(id+"F5.boolean.opBoolean","COPY",FACE,{"derivedFrom":makeQuery(id+"F5.opExtrude","SWEPT_FACE",FACE,{"disambiguationData":[OSD([sQuery(id+"F4.wireOp",EDGE,"E8")])]})});
            circularPattern(context, id + "F9", {"operationType" : NewBodyOperationType.REMOVE, "entities" : qUnion([Q0]), "axis" : qUnion([Q1]), "angle" : 360 * degree, "instanceCount" : 6, "equalSpace" : true});
        }
        {
            var Q0;
            {var subQ0=sQuery(id+"F0.wireOp",EDGE,"E7");var subQ1=makeQuery(id+"F2.opExtrude","CAP_FACE",FACE,{"disambiguationData":[OSD([sQuery(id+"F0.wireOp",EDGE,"E2"),sQuery(id+"F0.wireOp",EDGE,"E3"),sQuery(id+"F0.wireOp",EDGE,"E4"),sQuery(id+"F0.wireOp",EDGE,"E5"),sQuery(id+"F0.wireOp",EDGE,"E6"),subQ0])],"isStart":false});Q0=makeQuery(id+"F3.boolean.opBoolean","MERGE",FACE,{"derivedFrom":[makeQuery(id+"F1.opExtrude","CAP_FACE",FACE,{"disambiguationData":[OSD([sQuery(id+"F0.wireOp",EDGE,"E0"),sQuery(id+"F0.wireOp",EDGE,"E1"),subQ0])],"isStart":false}),subQ1,makeQuery(id+"F3.opPattern","COPY",FACE,{"derivedFrom":subQ1,"instanceName":"1"}),makeQuery(id+"F3.opPattern","COPY",FACE,{"derivedFrom":subQ1,"instanceName":"2"}),makeQuery(id+"F3.opPattern","COPY",FACE,{"derivedFrom":subQ1,"instanceName":"3"}),makeQuery(id+"F3.opPattern","COPY",FACE,{"derivedFrom":subQ1,"instanceName":"4"}),makeQuery(id+"F3.opPattern","COPY",FACE,{"derivedFrom":subQ1,"instanceName":"5"}),makeQuery(id+"F3.opPattern","COPY",FACE,{"derivedFrom":subQ1,"instanceName":"6"}),makeQuery(id+"F3.opPattern","COPY",FACE,{"derivedFrom":subQ1,"instanceName":"7"}),makeQuery(id+"F3.opPattern","COPY",FACE,{"derivedFrom":subQ1,"instanceName":"8"}),makeQuery(id+"F3.opPattern","COPY",FACE,{"derivedFrom":subQ1,"instanceName":"9"}),makeQuery(id+"F3.opPattern","COPY",FACE,{"derivedFrom":subQ1,"instanceName":"10"}),makeQuery(id+"F3.opPattern","COPY",FACE,{"derivedFrom":subQ1,"instanceName":"11"}),makeQuery(id+"F3.opPattern","COPY",FACE,{"derivedFrom":subQ1,"instanceName":"12"}),makeQuery(id+"F3.opPattern","COPY",FACE,{"derivedFrom":subQ1,"instanceName":"13"}),makeQuery(id+"F3.opPattern","COPY",FACE,{"derivedFrom":subQ1,"instanceName":"14"}),makeQuery(id+"F3.opPattern","COPY",FACE,{"derivedFrom":subQ1,"instanceName":"15"}),makeQuery(id+"F3.opPattern","COPY",FACE,{"derivedFrom":subQ1,"instanceName":"16"}),makeQuery(id+"F3.opPattern","COPY",FACE,{"derivedFrom":subQ1,"instanceName":"17"}),makeQuery(id+"F3.opPattern","COPY",FACE,{"derivedFrom":subQ1,"instanceName":"18"}),makeQuery(id+"F3.opPattern","COPY",FACE,{"derivedFrom":subQ1,"instanceName":"19"}),makeQuery(id+"F3.opPattern","COPY",FACE,{"derivedFrom":subQ1,"instanceName":"20"}),makeQuery(id+"F3.opPattern","COPY",FACE,{"derivedFrom":subQ1,"instanceName":"21"}),makeQuery(id+"F3.opPattern","COPY",FACE,{"derivedFrom":subQ1,"instanceName":"22"}),makeQuery(id+"F3.opPattern","COPY",FACE,{"derivedFrom":subQ1,"instanceName":"23"}),makeQuery(id+"F3.opPattern","COPY",FACE,{"derivedFrom":subQ1,"instanceName":"24"}),makeQuery(id+"F3.opPattern","COPY",FACE,{"derivedFrom":subQ1,"instanceName":"25"}),makeQuery(id+"F3.opPattern","COPY",FACE,{"derivedFrom":subQ1,"instanceName":"26"}),makeQuery(id+"F3.opPattern","COPY",FACE,{"derivedFrom":subQ1,"instanceName":"27"}),makeQuery(id+"F3.opPattern","COPY",FACE,{"derivedFrom":subQ1,"instanceName":"28"}),makeQuery(id+"F3.opPattern","COPY",FACE,{"derivedFrom":subQ1,"instanceName":"29"}),makeQuery(id+"F3.opPattern","COPY",FACE,{"derivedFrom":subQ1,"instanceName":"30"}),makeQuery(id+"F3.opPattern","COPY",FACE,{"derivedFrom":subQ1,"instanceName":"31"}),makeQuery(id+"F3.opPattern","COPY",FACE,{"derivedFrom":subQ1,"instanceName":"32"}),makeQuery(id+"F3.opPattern","COPY",FACE,{"derivedFrom":subQ1,"instanceName":"33"}),makeQuery(id+"F3.opPattern","COPY",FACE,{"derivedFrom":subQ1,"instanceName":"34"}),makeQuery(id+"F3.opPattern","COPY",FACE,{"derivedFrom":subQ1,"instanceName":"35"}),makeQuery(id+"F3.opPattern","COPY",FACE,{"derivedFrom":subQ1,"instanceName":"36"}),makeQuery(id+"F3.opPattern","COPY",FACE,{"derivedFrom":subQ1,"instanceName":"37"}),makeQuery(id+"F3.opPattern","COPY",FACE,{"derivedFrom":subQ1,"instanceName":"38"}),makeQuery(id+"F3.opPattern","COPY",FACE,{"derivedFrom":subQ1,"instanceName":"39"}),makeQuery(id+"F3.opPattern","COPY",FACE,{"derivedFrom":subQ1,"instanceName":"40"}),makeQuery(id+"F3.opPattern","COPY",FACE,{"derivedFrom":subQ1,"instanceName":"41"}),makeQuery(id+"F3.opPattern","COPY",FACE,{"derivedFrom":subQ1,"instanceName":"42"}),makeQuery(id+"F3.opPattern","COPY",FACE,{"derivedFrom":subQ1,"instanceName":"43"}),makeQuery(id+"F3.opPattern","COPY",FACE,{"derivedFrom":subQ1,"instanceName":"44"}),makeQuery(id+"F3.opPattern","COPY",FACE,{"derivedFrom":subQ1,"instanceName":"45"}),makeQuery(id+"F3.opPattern","COPY",FACE,{"derivedFrom":subQ1,"instanceName":"46"}),makeQuery(id+"F3.opPattern","COPY",FACE,{"derivedFrom":subQ1,"instanceName":"47"}),makeQuery(id+"F3.opPattern","COPY",FACE,{"derivedFrom":subQ1,"instanceName":"48"}),makeQuery(id+"F3.opPattern","COPY",FACE,{"derivedFrom":subQ1,"instanceName":"49"}),makeQuery(id+"F3.opPattern","COPY",FACE,{"derivedFrom":subQ1,"instanceName":"50"}),makeQuery(id+"F3.opPattern","COPY",FACE,{"derivedFrom":subQ1,"instanceName":"51"}),makeQuery(id+"F3.opPattern","COPY",FACE,{"derivedFrom":subQ1,"instanceName":"52"}),makeQuery(id+"F3.opPattern","COPY",FACE,{"derivedFrom":subQ1,"instanceName":"53"}),makeQuery(id+"F3.opPattern","COPY",FACE,{"derivedFrom":subQ1,"instanceName":"54"}),makeQuery(id+"F3.opPattern","COPY",FACE,{"derivedFrom":subQ1,"instanceName":"55"}),makeQuery(id+"F3.opPattern","COPY",FACE,{"derivedFrom":subQ1,"instanceName":"56"}),makeQuery(id+"F3.opPattern","COPY",FACE,{"derivedFrom":subQ1,"instanceName":"57"}),makeQuery(id+"F3.opPattern","COPY",FACE,{"derivedFrom":subQ1,"instanceName":"58"}),makeQuery(id+"F3.opPattern","COPY",FACE,{"derivedFrom":subQ1,"instanceName":"59"}),makeQuery(id+"F3.opPattern","COPY",FACE,{"derivedFrom":subQ1,"instanceName":"60"}),makeQuery(id+"F3.opPattern","COPY",FACE,{"derivedFrom":subQ1,"instanceName":"61"}),makeQuery(id+"F3.opPattern","COPY",FACE,{"derivedFrom":subQ1,"instanceName":"62"}),makeQuery(id+"F3.opPattern","COPY",FACE,{"derivedFrom":subQ1,"instanceName":"63"}),makeQuery(id+"F3.opPattern","COPY",FACE,{"derivedFrom":subQ1,"instanceName":"64"}),makeQuery(id+"F3.opPattern","COPY",FACE,{"derivedFrom":subQ1,"instanceName":"65"}),makeQuery(id+"F3.opPattern","COPY",FACE,{"derivedFrom":subQ1,"instanceName":"66"}),makeQuery(id+"F3.opPattern","COPY",FACE,{"derivedFrom":subQ1,"instanceName":"67"}),makeQuery(id+"F3.opPattern","COPY",FACE,{"derivedFrom":subQ1,"instanceName":"68"}),makeQuery(id+"F3.opPattern","COPY",FACE,{"derivedFrom":subQ1,"instanceName":"69"}),makeQuery(id+"F3.opPattern","COPY",FACE,{"derivedFrom":subQ1,"instanceName":"70"}),makeQuery(id+"F3.opPattern","COPY",FACE,{"derivedFrom":subQ1,"instanceName":"71"}),makeQuery(id+"F3.opPattern","COPY",FACE,{"derivedFrom":subQ1,"instanceName":"72"}),makeQuery(id+"F3.opPattern","COPY",FACE,{"derivedFrom":subQ1,"instanceName":"73"}),makeQuery(id+"F3.opPattern","COPY",FACE,{"derivedFrom":subQ1,"instanceName":"74"}),makeQuery(id+"F3.opPattern","COPY",FACE,{"derivedFrom":subQ1,"instanceName":"75"}),makeQuery(id+"F3.opPattern","COPY",FACE,{"derivedFrom":subQ1,"instanceName":"76"}),makeQuery(id+"F3.opPattern","COPY",FACE,{"derivedFrom":subQ1,"instanceName":"77"}),makeQuery(id+"F3.opPattern","COPY",FACE,{"derivedFrom":subQ1,"instanceName":"78"}),makeQuery(id+"F3.opPattern","COPY",FACE,{"derivedFrom":subQ1,"instanceName":"79"}),makeQuery(id+"F3.opPattern","COPY",FACE,{"derivedFrom":subQ1,"instanceName":"80"}),makeQuery(id+"F3.opPattern","COPY",FACE,{"derivedFrom":subQ1,"instanceName":"81"}),makeQuery(id+"F3.opPattern","COPY",FACE,{"derivedFrom":subQ1,"instanceName":"82"}),makeQuery(id+"F3.opPattern","COPY",FACE,{"derivedFrom":subQ1,"instanceName":"83"}),makeQuery(id+"F3.opPattern","COPY",FACE,{"derivedFrom":subQ1,"instanceName":"84"}),makeQuery(id+"F3.opPattern","COPY",FACE,{"derivedFrom":subQ1,"instanceName":"85"}),makeQuery(id+"F3.opPattern","COPY",FACE,{"derivedFrom":subQ1,"instanceName":"86"}),makeQuery(id+"F3.opPattern","COPY",FACE,{"derivedFrom":subQ1,"instanceName":"87"}),makeQuery(id+"F3.opPattern","COPY",FACE,{"derivedFrom":subQ1,"instanceName":"88"}),makeQuery(id+"F3.opPattern","COPY",FACE,{"derivedFrom":subQ1,"instanceName":"89"}),makeQuery(id+"F3.opPattern","COPY",FACE,{"derivedFrom":subQ1,"instanceName":"90"}),makeQuery(id+"F3.opPattern","COPY",FACE,{"derivedFrom":subQ1,"instanceName":"91"}),makeQuery(id+"F3.opPattern","COPY",FACE,{"derivedFrom":subQ1,"instanceName":"92"}),makeQuery(id+"F3.opPattern","COPY",FACE,{"derivedFrom":subQ1,"instanceName":"93"}),makeQuery(id+"F3.opPattern","COPY",FACE,{"derivedFrom":subQ1,"instanceName":"94"}),makeQuery(id+"F3.opPattern","COPY",FACE,{"derivedFrom":subQ1,"instanceName":"95"}),makeQuery(id+"F3.opPattern","COPY",FACE,{"derivedFrom":subQ1,"instanceName":"96"}),makeQuery(id+"F3.opPattern","COPY",FACE,{"derivedFrom":subQ1,"instanceName":"97"}),makeQuery(id+"F3.opPattern","COPY",FACE,{"derivedFrom":subQ1,"instanceName":"98"}),makeQuery(id+"F3.opPattern","COPY",FACE,{"derivedFrom":subQ1,"instanceName":"99"}),makeQuery(id+"F3.opPattern","COPY",FACE,{"derivedFrom":subQ1,"instanceName":"100"}),makeQuery(id+"F3.opPattern","COPY",FACE,{"derivedFrom":subQ1,"instanceName":"101"}),makeQuery(id+"F3.opPattern","COPY",FACE,{"derivedFrom":subQ1,"instanceName":"102"}),makeQuery(id+"F3.opPattern","COPY",FACE,{"derivedFrom":subQ1,"instanceName":"103"}),makeQuery(id+"F3.opPattern","COPY",FACE,{"derivedFrom":subQ1,"instanceName":"104"}),makeQuery(id+"F3.opPattern","COPY",FACE,{"derivedFrom":subQ1,"instanceName":"105"}),makeQuery(id+"F3.opPattern","COPY",FACE,{"derivedFrom":subQ1,"instanceName":"106"}),makeQuery(id+"F3.opPattern","COPY",FACE,{"derivedFrom":subQ1,"instanceName":"107"}),makeQuery(id+"F3.opPattern","COPY",FACE,{"derivedFrom":subQ1,"instanceName":"108"}),makeQuery(id+"F3.opPattern","COPY",FACE,{"derivedFrom":subQ1,"instanceName":"109"}),makeQuery(id+"F3.opPattern","COPY",FACE,{"derivedFrom":subQ1,"instanceName":"110"}),makeQuery(id+"F3.opPattern","COPY",FACE,{"derivedFrom":subQ1,"instanceName":"111"}),makeQuery(id+"F3.opPattern","COPY",FACE,{"derivedFrom":subQ1,"instanceName":"112"}),makeQuery(id+"F3.opPattern","COPY",FACE,{"derivedFrom":subQ1,"instanceName":"113"}),makeQuery(id+"F3.opPattern","COPY",FACE,{"derivedFrom":subQ1,"instanceName":"114"}),makeQuery(id+"F3.opPattern","COPY",FACE,{"derivedFrom":subQ1,"instanceName":"115"}),makeQuery(id+"F3.opPattern","COPY",FACE,{"derivedFrom":subQ1,"instanceName":"116"}),makeQuery(id+"F3.opPattern","COPY",FACE,{"derivedFrom":subQ1,"instanceName":"117"}),makeQuery(id+"F3.opPattern","COPY",FACE,{"derivedFrom":subQ1,"instanceName":"118"}),makeQuery(id+"F3.opPattern","COPY",FACE,{"derivedFrom":subQ1,"instanceName":"119"}),makeQuery(id+"F3.opPattern","COPY",FACE,{"derivedFrom":subQ1,"instanceName":"120"}),makeQuery(id+"F3.opPattern","COPY",FACE,{"derivedFrom":subQ1,"instanceName":"121"}),makeQuery(id+"F3.opPattern","COPY",FACE,{"derivedFrom":subQ1,"instanceName":"122"}),makeQuery(id+"F3.opPattern","COPY",FACE,{"derivedFrom":subQ1,"instanceName":"123"}),makeQuery(id+"F3.opPattern","COPY",FACE,{"derivedFrom":subQ1,"instanceName":"124"}),makeQuery(id+"F3.opPattern","COPY",FACE,{"derivedFrom":subQ1,"instanceName":"125"}),makeQuery(id+"F3.opPattern","COPY",FACE,{"derivedFrom":subQ1,"instanceName":"126"}),makeQuery(id+"F3.opPattern","COPY",FACE,{"derivedFrom":subQ1,"instanceName":"127"}),makeQuery(id+"F3.opPattern","COPY",FACE,{"derivedFrom":subQ1,"instanceName":"128"}),makeQuery(id+"F3.opPattern","COPY",FACE,{"derivedFrom":subQ1,"instanceName":"129"}),makeQuery(id+"F3.opPattern","COPY",FACE,{"derivedFrom":subQ1,"instanceName":"130"}),makeQuery(id+"F3.opPattern","COPY",FACE,{"derivedFrom":subQ1,"instanceName":"131"})]});}
            var sketch = newSketch(context, id + "F10", { "sketchPlane" : qUnion([Q0])});
            skArc(sketch, "E27", {"start": v(-10.66, 28.02) * mm, "mid": v(-14.99, 25.96) * mm, "end": v(-18.93, 23.24) * mm});
            skArc(sketch, "E28.0", {"start": v(18.93, 23.24) * mm, "mid": v(19.25, 11.11) * mm, "end": v(29.6, 4.78) * mm});
            skArc(sketch, "E29.0", {"start": v(-10.66, 28.02) * mm, "mid": v(0, 22.23) * mm, "end": v(10.66, 28.02) * mm});
            skArc(sketch, "E29.1", {"start": v(-29.78, 4.77) * mm, "mid": v(-19.25, 11.11) * mm, "end": v(-19.02, 23.4) * mm});
            skArc(sketch, "E29.2", {"start": v(-18.93, -23.24) * mm, "mid": v(-19.25, -11.11) * mm, "end": v(-29.6, -4.78) * mm});
            skArc(sketch, "E29.3", {"start": v(10.66, -28.02) * mm, "mid": v(0, -22.23) * mm, "end": v(-10.66, -28.02) * mm});
            skArc(sketch, "E29.4", {"start": v(29.6, -4.78) * mm, "mid": v(19.25, -11.11) * mm, "end": v(18.93, -23.24) * mm});
            skArc(sketch, "E30.trimOffspring", {"start": v(18.93, 23.24) * mm, "mid": v(14.99, 25.96) * mm, "end": v(10.66, 28.02) * mm});
            skArc(sketch, "E31.trimOffspring", {"start": v(29.6, -4.78) * mm, "mid": v(29.97, 0) * mm, "end": v(29.6, 4.78) * mm});
            skArc(sketch, "E32.trimOffspring", {"start": v(10.66, -28.02) * mm, "mid": v(14.99, -25.96) * mm, "end": v(18.93, -23.24) * mm});
            skArc(sketch, "E33.trimOffspring", {"start": v(-18.93, -23.24) * mm, "mid": v(-14.99, -25.96) * mm, "end": v(-10.66, -28.02) * mm});
            skArc(sketch, "E34.trimOffspring", {"start": v(-29.6, 4.78) * mm, "mid": v(-29.97, 0) * mm, "end": v(-29.6, -4.78) * mm});
            skCircle(sketch, "E35.0", {"center": v(-11.9, 20.62) * mm, "radius": 2.41 * mm});
            skCircle(sketch, "E35.1", {"center": v(11.9, 20.62) * mm, "radius": 2.41 * mm});
            skCircle(sketch, "E35.2", {"center": v(23.81, 0) * mm, "radius": 2.41 * mm});
            skCircle(sketch, "E35.3", {"center": v(11.9, -20.62) * mm, "radius": 2.41 * mm});
            skCircle(sketch, "E35.4", {"center": v(-11.9, -20.62) * mm, "radius": 2.41 * mm});
            skCircle(sketch, "E35.5", {"center": v(-23.81, 0) * mm, "radius": 2.41 * mm});
            skCircle(sketch, "E36.0", {"center": v(0, 0) * mm, "radius": 14.29 * mm});
            skSolve(sketch);
        }
        {
            var Q0;
            Q0 = qSketchRegion(id + "F10", true);
            extrude(context, id + "F11", {"entities" : qUnion([Q0]), "depth" : 3.17 * mm});
        }
        {
            var Q0;
            Q0=makeQuery(id+"F11.opExtrude","SWEPT_EDGE",EDGE,{"disambiguationData":[OSD([sQuery(id+"F6.wireOp",EDGE,"E16"),sQuery(id+"F6.wireOp",EDGE,"E17"),sQuery(id+"F6.wireOp",EDGE,"E21.0"),sQuery(id+"F6.wireOp",EDGE,"E22.0"),sQuery(id+"F6.wireOp",EDGE,"E24"),sQuery(id+"F10.wireOp",EDGE,"E28.0"),sQuery(id+"F10.wireOp",EDGE,"E30.trimOffspring")])]});
            var Q1;
            Q1=makeQuery(id+"F11.opExtrude","SWEPT_EDGE",EDGE,{"disambiguationData":[OSD([sQuery(id+"F6.wireOp",EDGE,"E16"),sQuery(id+"F6.wireOp",EDGE,"E17"),sQuery(id+"F6.wireOp",EDGE,"E21.0"),sQuery(id+"F6.wireOp",EDGE,"E22.0"),sQuery(id+"F6.wireOp",EDGE,"E24"),sQuery(id+"F10.wireOp",EDGE,"E28.0"),sQuery(id+"F10.wireOp",EDGE,"E31.trimOffspring")])]});
            var Q2;
            Q2=makeQuery(id+"F11.opExtrude","SWEPT_EDGE",EDGE,{"disambiguationData":[OSD([sQuery(id+"F6.wireOp",EDGE,"E16"),sQuery(id+"F6.wireOp",EDGE,"E17"),sQuery(id+"F6.wireOp",EDGE,"E21.0"),sQuery(id+"F6.wireOp",EDGE,"E22.0"),sQuery(id+"F6.wireOp",EDGE,"E24"),sQuery(id+"F10.wireOp",EDGE,"E29.4"),sQuery(id+"F10.wireOp",EDGE,"E31.trimOffspring")])]});
            var Q3;
            Q3=makeQuery(id+"F11.opExtrude","SWEPT_EDGE",EDGE,{"disambiguationData":[OSD([sQuery(id+"F6.wireOp",EDGE,"E16"),sQuery(id+"F6.wireOp",EDGE,"E17"),sQuery(id+"F6.wireOp",EDGE,"E21.0"),sQuery(id+"F6.wireOp",EDGE,"E22.0"),sQuery(id+"F6.wireOp",EDGE,"E24"),sQuery(id+"F10.wireOp",EDGE,"E29.4"),sQuery(id+"F10.wireOp",EDGE,"E32.trimOffspring")])]});
            var Q4;
            Q4=makeQuery(id+"F11.opExtrude","SWEPT_EDGE",EDGE,{"disambiguationData":[OSD([sQuery(id+"F6.wireOp",EDGE,"E16"),sQuery(id+"F6.wireOp",EDGE,"E17"),sQuery(id+"F6.wireOp",EDGE,"E21.0"),sQuery(id+"F6.wireOp",EDGE,"E22.0"),sQuery(id+"F6.wireOp",EDGE,"E24"),sQuery(id+"F10.wireOp",EDGE,"E29.3"),sQuery(id+"F10.wireOp",EDGE,"E32.trimOffspring")])]});
            var Q5;
            Q5=makeQuery(id+"F11.opExtrude","SWEPT_EDGE",EDGE,{"disambiguationData":[OSD([sQuery(id+"F6.wireOp",EDGE,"E16"),sQuery(id+"F6.wireOp",EDGE,"E17"),sQuery(id+"F6.wireOp",EDGE,"E21.0"),sQuery(id+"F6.wireOp",EDGE,"E22.0"),sQuery(id+"F6.wireOp",EDGE,"E24"),sQuery(id+"F10.wireOp",EDGE,"E29.3"),sQuery(id+"F10.wireOp",EDGE,"E33.trimOffspring")])]});
            var Q6;
            Q6=makeQuery(id+"F11.opExtrude","SWEPT_EDGE",EDGE,{"disambiguationData":[OSD([sQuery(id+"F6.wireOp",EDGE,"E16"),sQuery(id+"F6.wireOp",EDGE,"E17"),sQuery(id+"F6.wireOp",EDGE,"E21.0"),sQuery(id+"F6.wireOp",EDGE,"E22.0"),sQuery(id+"F6.wireOp",EDGE,"E24"),sQuery(id+"F10.wireOp",EDGE,"E29.2"),sQuery(id+"F10.wireOp",EDGE,"E33.trimOffspring")])]});
            var Q7;
            Q7=makeQuery(id+"F11.opExtrude","SWEPT_EDGE",EDGE,{"disambiguationData":[OSD([sQuery(id+"F6.wireOp",EDGE,"E16"),sQuery(id+"F6.wireOp",EDGE,"E17"),sQuery(id+"F6.wireOp",EDGE,"E21.0"),sQuery(id+"F6.wireOp",EDGE,"E22.0"),sQuery(id+"F6.wireOp",EDGE,"E24"),sQuery(id+"F10.wireOp",EDGE,"E29.2"),sQuery(id+"F10.wireOp",EDGE,"E34.trimOffspring")])]});
            var Q8;
            Q8=makeQuery(id+"F11.opExtrude","SWEPT_EDGE",EDGE,{"disambiguationData":[OSD([sQuery(id+"F6.wireOp",EDGE,"E16"),sQuery(id+"F6.wireOp",EDGE,"E17"),sQuery(id+"F6.wireOp",EDGE,"E21.0"),sQuery(id+"F6.wireOp",EDGE,"E22.0"),sQuery(id+"F6.wireOp",EDGE,"E24"),sQuery(id+"F10.wireOp",EDGE,"E29.1"),sQuery(id+"F10.wireOp",EDGE,"E34.trimOffspring")])]});
            var Q9;
            Q9=makeQuery(id+"F11.opExtrude","SWEPT_EDGE",EDGE,{"disambiguationData":[OSD([sQuery(id+"F6.wireOp",EDGE,"E16"),sQuery(id+"F6.wireOp",EDGE,"E17"),sQuery(id+"F6.wireOp",EDGE,"E21.0"),sQuery(id+"F6.wireOp",EDGE,"E22.0"),sQuery(id+"F6.wireOp",EDGE,"E24"),sQuery(id+"F10.wireOp",EDGE,"E27"),sQuery(id+"F10.wireOp",EDGE,"E29.1")])]});
            var Q10;
            Q10=makeQuery(id+"F11.opExtrude","SWEPT_EDGE",EDGE,{"disambiguationData":[OSD([sQuery(id+"F6.wireOp",EDGE,"E16"),sQuery(id+"F6.wireOp",EDGE,"E17"),sQuery(id+"F6.wireOp",EDGE,"E21.0"),sQuery(id+"F6.wireOp",EDGE,"E22.0"),sQuery(id+"F6.wireOp",EDGE,"E24"),sQuery(id+"F10.wireOp",EDGE,"E27"),sQuery(id+"F10.wireOp",EDGE,"E29.0")])]});
            var Q11;
            Q11=makeQuery(id+"F11.opExtrude","SWEPT_EDGE",EDGE,{"disambiguationData":[OSD([sQuery(id+"F6.wireOp",EDGE,"E16"),sQuery(id+"F6.wireOp",EDGE,"E17"),sQuery(id+"F6.wireOp",EDGE,"E21.0"),sQuery(id+"F6.wireOp",EDGE,"E22.0"),sQuery(id+"F6.wireOp",EDGE,"E24"),sQuery(id+"F10.wireOp",EDGE,"E29.0"),sQuery(id+"F10.wireOp",EDGE,"E30.trimOffspring")])]});
            fillet(context, id + "F12", {"entities" : qUnion([Q0, Q1, Q2, Q3, Q4, Q5, Q6, Q7, Q8, Q9, Q10, Q11]), "radius" : 1.59 * mm, "tangentPropagation" : true, "allowEdgeOverflow" : false});
        }
        {
            var Q0;
            {var subQ0=sQuery(id+"F0.wireOp",EDGE,"E7");var subQ1=makeQuery(id+"F2.opExtrude","CAP_FACE",FACE,{"disambiguationData":[OSD([sQuery(id+"F0.wireOp",EDGE,"E2"),sQuery(id+"F0.wireOp",EDGE,"E3"),sQuery(id+"F0.wireOp",EDGE,"E4"),sQuery(id+"F0.wireOp",EDGE,"E5"),sQuery(id+"F0.wireOp",EDGE,"E6"),subQ0])],"isStart":true});Q0=makeQuery(id+"F3.boolean.opBoolean","MERGE",FACE,{"derivedFrom":[makeQuery(id+"F1.opExtrude","CAP_FACE",FACE,{"disambiguationData":[OSD([sQuery(id+"F0.wireOp",EDGE,"E0"),sQuery(id+"F0.wireOp",EDGE,"E1"),subQ0])],"isStart":true}),subQ1,makeQuery(id+"F3.opPattern","COPY",FACE,{"derivedFrom":subQ1,"instanceName":"1"}),makeQuery(id+"F3.opPattern","COPY",FACE,{"derivedFrom":subQ1,"instanceName":"2"}),makeQuery(id+"F3.opPattern","COPY",FACE,{"derivedFrom":subQ1,"instanceName":"3"}),makeQuery(id+"F3.opPattern","COPY",FACE,{"derivedFrom":subQ1,"instanceName":"4"}),makeQuery(id+"F3.opPattern","COPY",FACE,{"derivedFrom":subQ1,"instanceName":"5"}),makeQuery(id+"F3.opPattern","COPY",FACE,{"derivedFrom":subQ1,"instanceName":"6"}),makeQuery(id+"F3.opPattern","COPY",FACE,{"derivedFrom":subQ1,"instanceName":"7"}),makeQuery(id+"F3.opPattern","COPY",FACE,{"derivedFrom":subQ1,"instanceName":"8"}),makeQuery(id+"F3.opPattern","COPY",FACE,{"derivedFrom":subQ1,"instanceName":"9"}),makeQuery(id+"F3.opPattern","COPY",FACE,{"derivedFrom":subQ1,"instanceName":"10"}),makeQuery(id+"F3.opPattern","COPY",FACE,{"derivedFrom":subQ1,"instanceName":"11"}),makeQuery(id+"F3.opPattern","COPY",FACE,{"derivedFrom":subQ1,"instanceName":"12"}),makeQuery(id+"F3.opPattern","COPY",FACE,{"derivedFrom":subQ1,"instanceName":"13"}),makeQuery(id+"F3.opPattern","COPY",FACE,{"derivedFrom":subQ1,"instanceName":"14"}),makeQuery(id+"F3.opPattern","COPY",FACE,{"derivedFrom":subQ1,"instanceName":"15"}),makeQuery(id+"F3.opPattern","COPY",FACE,{"derivedFrom":subQ1,"instanceName":"16"}),makeQuery(id+"F3.opPattern","COPY",FACE,{"derivedFrom":subQ1,"instanceName":"17"}),makeQuery(id+"F3.opPattern","COPY",FACE,{"derivedFrom":subQ1,"instanceName":"18"}),makeQuery(id+"F3.opPattern","COPY",FACE,{"derivedFrom":subQ1,"instanceName":"19"}),makeQuery(id+"F3.opPattern","COPY",FACE,{"derivedFrom":subQ1,"instanceName":"20"}),makeQuery(id+"F3.opPattern","COPY",FACE,{"derivedFrom":subQ1,"instanceName":"21"}),makeQuery(id+"F3.opPattern","COPY",FACE,{"derivedFrom":subQ1,"instanceName":"22"}),makeQuery(id+"F3.opPattern","COPY",FACE,{"derivedFrom":subQ1,"instanceName":"23"}),makeQuery(id+"F3.opPattern","COPY",FACE,{"derivedFrom":subQ1,"instanceName":"24"}),makeQuery(id+"F3.opPattern","COPY",FACE,{"derivedFrom":subQ1,"instanceName":"25"}),makeQuery(id+"F3.opPattern","COPY",FACE,{"derivedFrom":subQ1,"instanceName":"26"}),makeQuery(id+"F3.opPattern","COPY",FACE,{"derivedFrom":subQ1,"instanceName":"27"}),makeQuery(id+"F3.opPattern","COPY",FACE,{"derivedFrom":subQ1,"instanceName":"28"}),makeQuery(id+"F3.opPattern","COPY",FACE,{"derivedFrom":subQ1,"instanceName":"29"}),makeQuery(id+"F3.opPattern","COPY",FACE,{"derivedFrom":subQ1,"instanceName":"30"}),makeQuery(id+"F3.opPattern","COPY",FACE,{"derivedFrom":subQ1,"instanceName":"31"}),makeQuery(id+"F3.opPattern","COPY",FACE,{"derivedFrom":subQ1,"instanceName":"32"}),makeQuery(id+"F3.opPattern","COPY",FACE,{"derivedFrom":subQ1,"instanceName":"33"}),makeQuery(id+"F3.opPattern","COPY",FACE,{"derivedFrom":subQ1,"instanceName":"34"}),makeQuery(id+"F3.opPattern","COPY",FACE,{"derivedFrom":subQ1,"instanceName":"35"}),makeQuery(id+"F3.opPattern","COPY",FACE,{"derivedFrom":subQ1,"instanceName":"36"}),makeQuery(id+"F3.opPattern","COPY",FACE,{"derivedFrom":subQ1,"instanceName":"37"}),makeQuery(id+"F3.opPattern","COPY",FACE,{"derivedFrom":subQ1,"instanceName":"38"}),makeQuery(id+"F3.opPattern","COPY",FACE,{"derivedFrom":subQ1,"instanceName":"39"}),makeQuery(id+"F3.opPattern","COPY",FACE,{"derivedFrom":subQ1,"instanceName":"40"}),makeQuery(id+"F3.opPattern","COPY",FACE,{"derivedFrom":subQ1,"instanceName":"41"}),makeQuery(id+"F3.opPattern","COPY",FACE,{"derivedFrom":subQ1,"instanceName":"42"}),makeQuery(id+"F3.opPattern","COPY",FACE,{"derivedFrom":subQ1,"instanceName":"43"}),makeQuery(id+"F3.opPattern","COPY",FACE,{"derivedFrom":subQ1,"instanceName":"44"}),makeQuery(id+"F3.opPattern","COPY",FACE,{"derivedFrom":subQ1,"instanceName":"45"}),makeQuery(id+"F3.opPattern","COPY",FACE,{"derivedFrom":subQ1,"instanceName":"46"}),makeQuery(id+"F3.opPattern","COPY",FACE,{"derivedFrom":subQ1,"instanceName":"47"}),makeQuery(id+"F3.opPattern","COPY",FACE,{"derivedFrom":subQ1,"instanceName":"48"}),makeQuery(id+"F3.opPattern","COPY",FACE,{"derivedFrom":subQ1,"instanceName":"49"}),makeQuery(id+"F3.opPattern","COPY",FACE,{"derivedFrom":subQ1,"instanceName":"50"}),makeQuery(id+"F3.opPattern","COPY",FACE,{"derivedFrom":subQ1,"instanceName":"51"}),makeQuery(id+"F3.opPattern","COPY",FACE,{"derivedFrom":subQ1,"instanceName":"52"}),makeQuery(id+"F3.opPattern","COPY",FACE,{"derivedFrom":subQ1,"instanceName":"53"}),makeQuery(id+"F3.opPattern","COPY",FACE,{"derivedFrom":subQ1,"instanceName":"54"}),makeQuery(id+"F3.opPattern","COPY",FACE,{"derivedFrom":subQ1,"instanceName":"55"}),makeQuery(id+"F3.opPattern","COPY",FACE,{"derivedFrom":subQ1,"instanceName":"56"}),makeQuery(id+"F3.opPattern","COPY",FACE,{"derivedFrom":subQ1,"instanceName":"57"}),makeQuery(id+"F3.opPattern","COPY",FACE,{"derivedFrom":subQ1,"instanceName":"58"}),makeQuery(id+"F3.opPattern","COPY",FACE,{"derivedFrom":subQ1,"instanceName":"59"}),makeQuery(id+"F3.opPattern","COPY",FACE,{"derivedFrom":subQ1,"instanceName":"60"}),makeQuery(id+"F3.opPattern","COPY",FACE,{"derivedFrom":subQ1,"instanceName":"61"}),makeQuery(id+"F3.opPattern","COPY",FACE,{"derivedFrom":subQ1,"instanceName":"62"}),makeQuery(id+"F3.opPattern","COPY",FACE,{"derivedFrom":subQ1,"instanceName":"63"}),makeQuery(id+"F3.opPattern","COPY",FACE,{"derivedFrom":subQ1,"instanceName":"64"}),makeQuery(id+"F3.opPattern","COPY",FACE,{"derivedFrom":subQ1,"instanceName":"65"}),makeQuery(id+"F3.opPattern","COPY",FACE,{"derivedFrom":subQ1,"instanceName":"66"}),makeQuery(id+"F3.opPattern","COPY",FACE,{"derivedFrom":subQ1,"instanceName":"67"}),makeQuery(id+"F3.opPattern","COPY",FACE,{"derivedFrom":subQ1,"instanceName":"68"}),makeQuery(id+"F3.opPattern","COPY",FACE,{"derivedFrom":subQ1,"instanceName":"69"}),makeQuery(id+"F3.opPattern","COPY",FACE,{"derivedFrom":subQ1,"instanceName":"70"}),makeQuery(id+"F3.opPattern","COPY",FACE,{"derivedFrom":subQ1,"instanceName":"71"}),makeQuery(id+"F3.opPattern","COPY",FACE,{"derivedFrom":subQ1,"instanceName":"72"}),makeQuery(id+"F3.opPattern","COPY",FACE,{"derivedFrom":subQ1,"instanceName":"73"}),makeQuery(id+"F3.opPattern","COPY",FACE,{"derivedFrom":subQ1,"instanceName":"74"}),makeQuery(id+"F3.opPattern","COPY",FACE,{"derivedFrom":subQ1,"instanceName":"75"}),makeQuery(id+"F3.opPattern","COPY",FACE,{"derivedFrom":subQ1,"instanceName":"76"}),makeQuery(id+"F3.opPattern","COPY",FACE,{"derivedFrom":subQ1,"instanceName":"77"}),makeQuery(id+"F3.opPattern","COPY",FACE,{"derivedFrom":subQ1,"instanceName":"78"}),makeQuery(id+"F3.opPattern","COPY",FACE,{"derivedFrom":subQ1,"instanceName":"79"}),makeQuery(id+"F3.opPattern","COPY",FACE,{"derivedFrom":subQ1,"instanceName":"80"}),makeQuery(id+"F3.opPattern","COPY",FACE,{"derivedFrom":subQ1,"instanceName":"81"}),makeQuery(id+"F3.opPattern","COPY",FACE,{"derivedFrom":subQ1,"instanceName":"82"}),makeQuery(id+"F3.opPattern","COPY",FACE,{"derivedFrom":subQ1,"instanceName":"83"}),makeQuery(id+"F3.opPattern","COPY",FACE,{"derivedFrom":subQ1,"instanceName":"84"}),makeQuery(id+"F3.opPattern","COPY",FACE,{"derivedFrom":subQ1,"instanceName":"85"}),makeQuery(id+"F3.opPattern","COPY",FACE,{"derivedFrom":subQ1,"instanceName":"86"}),makeQuery(id+"F3.opPattern","COPY",FACE,{"derivedFrom":subQ1,"instanceName":"87"}),makeQuery(id+"F3.opPattern","COPY",FACE,{"derivedFrom":subQ1,"instanceName":"88"}),makeQuery(id+"F3.opPattern","COPY",FACE,{"derivedFrom":subQ1,"instanceName":"89"}),makeQuery(id+"F3.opPattern","COPY",FACE,{"derivedFrom":subQ1,"instanceName":"90"}),makeQuery(id+"F3.opPattern","COPY",FACE,{"derivedFrom":subQ1,"instanceName":"91"}),makeQuery(id+"F3.opPattern","COPY",FACE,{"derivedFrom":subQ1,"instanceName":"92"}),makeQuery(id+"F3.opPattern","COPY",FACE,{"derivedFrom":subQ1,"instanceName":"93"}),makeQuery(id+"F3.opPattern","COPY",FACE,{"derivedFrom":subQ1,"instanceName":"94"}),makeQuery(id+"F3.opPattern","COPY",FACE,{"derivedFrom":subQ1,"instanceName":"95"}),makeQuery(id+"F3.opPattern","COPY",FACE,{"derivedFrom":subQ1,"instanceName":"96"}),makeQuery(id+"F3.opPattern","COPY",FACE,{"derivedFrom":subQ1,"instanceName":"97"}),makeQuery(id+"F3.opPattern","COPY",FACE,{"derivedFrom":subQ1,"instanceName":"98"}),makeQuery(id+"F3.opPattern","COPY",FACE,{"derivedFrom":subQ1,"instanceName":"99"}),makeQuery(id+"F3.opPattern","COPY",FACE,{"derivedFrom":subQ1,"instanceName":"100"}),makeQuery(id+"F3.opPattern","COPY",FACE,{"derivedFrom":subQ1,"instanceName":"101"}),makeQuery(id+"F3.opPattern","COPY",FACE,{"derivedFrom":subQ1,"instanceName":"102"}),makeQuery(id+"F3.opPattern","COPY",FACE,{"derivedFrom":subQ1,"instanceName":"103"}),makeQuery(id+"F3.opPattern","COPY",FACE,{"derivedFrom":subQ1,"instanceName":"104"}),makeQuery(id+"F3.opPattern","COPY",FACE,{"derivedFrom":subQ1,"instanceName":"105"}),makeQuery(id+"F3.opPattern","COPY",FACE,{"derivedFrom":subQ1,"instanceName":"106"}),makeQuery(id+"F3.opPattern","COPY",FACE,{"derivedFrom":subQ1,"instanceName":"107"}),makeQuery(id+"F3.opPattern","COPY",FACE,{"derivedFrom":subQ1,"instanceName":"108"}),makeQuery(id+"F3.opPattern","COPY",FACE,{"derivedFrom":subQ1,"instanceName":"109"}),makeQuery(id+"F3.opPattern","COPY",FACE,{"derivedFrom":subQ1,"instanceName":"110"}),makeQuery(id+"F3.opPattern","COPY",FACE,{"derivedFrom":subQ1,"instanceName":"111"}),makeQuery(id+"F3.opPattern","COPY",FACE,{"derivedFrom":subQ1,"instanceName":"112"}),makeQuery(id+"F3.opPattern","COPY",FACE,{"derivedFrom":subQ1,"instanceName":"113"}),makeQuery(id+"F3.opPattern","COPY",FACE,{"derivedFrom":subQ1,"instanceName":"114"}),makeQuery(id+"F3.opPattern","COPY",FACE,{"derivedFrom":subQ1,"instanceName":"115"}),makeQuery(id+"F3.opPattern","COPY",FACE,{"derivedFrom":subQ1,"instanceName":"116"}),makeQuery(id+"F3.opPattern","COPY",FACE,{"derivedFrom":subQ1,"instanceName":"117"}),makeQuery(id+"F3.opPattern","COPY",FACE,{"derivedFrom":subQ1,"instanceName":"118"}),makeQuery(id+"F3.opPattern","COPY",FACE,{"derivedFrom":subQ1,"instanceName":"119"}),makeQuery(id+"F3.opPattern","COPY",FACE,{"derivedFrom":subQ1,"instanceName":"120"}),makeQuery(id+"F3.opPattern","COPY",FACE,{"derivedFrom":subQ1,"instanceName":"121"}),makeQuery(id+"F3.opPattern","COPY",FACE,{"derivedFrom":subQ1,"instanceName":"122"}),makeQuery(id+"F3.opPattern","COPY",FACE,{"derivedFrom":subQ1,"instanceName":"123"}),makeQuery(id+"F3.opPattern","COPY",FACE,{"derivedFrom":subQ1,"instanceName":"124"}),makeQuery(id+"F3.opPattern","COPY",FACE,{"derivedFrom":subQ1,"instanceName":"125"}),makeQuery(id+"F3.opPattern","COPY",FACE,{"derivedFrom":subQ1,"instanceName":"126"}),makeQuery(id+"F3.opPattern","COPY",FACE,{"derivedFrom":subQ1,"instanceName":"127"}),makeQuery(id+"F3.opPattern","COPY",FACE,{"derivedFrom":subQ1,"instanceName":"128"}),makeQuery(id+"F3.opPattern","COPY",FACE,{"derivedFrom":subQ1,"instanceName":"129"}),makeQuery(id+"F3.opPattern","COPY",FACE,{"derivedFrom":subQ1,"instanceName":"130"}),makeQuery(id+"F3.opPattern","COPY",FACE,{"derivedFrom":subQ1,"instanceName":"131"})]});}
            var sketch = newSketch(context, id + "F13", { "sketchPlane" : qUnion([Q0])});
            skCircle(sketch, "E37.0", {"center": v(-23.81, 0) * mm, "radius": 2.41 * mm});
            skCircle(sketch, "E37.1", {"center": v(-11.9, 20.62) * mm, "radius": 2.41 * mm});
            skCircle(sketch, "E37.2", {"center": v(11.9, 20.62) * mm, "radius": 2.41 * mm});
            skCircle(sketch, "E37.3", {"center": v(23.81, 0) * mm, "radius": 2.41 * mm});
            skCircle(sketch, "E37.4", {"center": v(11.9, -20.62) * mm, "radius": 2.41 * mm});
            skCircle(sketch, "E37.5", {"center": v(-11.9, -20.62) * mm, "radius": 2.41 * mm});
            skSolve(sketch);
        }
        {
            var Q0;
            Q0=sQuery(id+"F13.wireOp",VERTEX,"E37.4.center");
            var Q1;
            Q1=sQuery(id+"F13.wireOp",VERTEX,"E37.3.center");
            var Q2;
            Q2=sQuery(id+"F13.wireOp",VERTEX,"E37.2.center");
            var Q3;
            Q3=sQuery(id+"F13.wireOp",VERTEX,"E37.1.center");
            var Q4;
            Q4=sQuery(id+"F13.wireOp",VERTEX,"E37.0.center");
            var Q5;
            Q5=sQuery(id+"F13.wireOp",VERTEX,"E37.5.center");
            var Q6;
            Q6=makeQuery(id+"F1.opExtrude","SWEPT_BODY",BODY,{"disambiguationData":[OSD([sQuery(id+"F0.wireOp",EDGE,"E0"),sQuery(id+"F0.wireOp",EDGE,"E1"),sQuery(id+"F0.wireOp",EDGE,"E7")])]});
            hole(context, id + "F14", {"style" : HoleStyle.C_BORE, "holeDiameter" : 4.83 * mm, "cBoreDiameter" : 7.94 * mm, "cBoreDepth" : 4.83 * mm, "endStyle" : HoleEndStyle.THROUGH, "locations" : qUnion([Q0, Q1, Q2, Q3, Q4, Q5]), "scope" : qUnion([Q6])});
        }
    });
